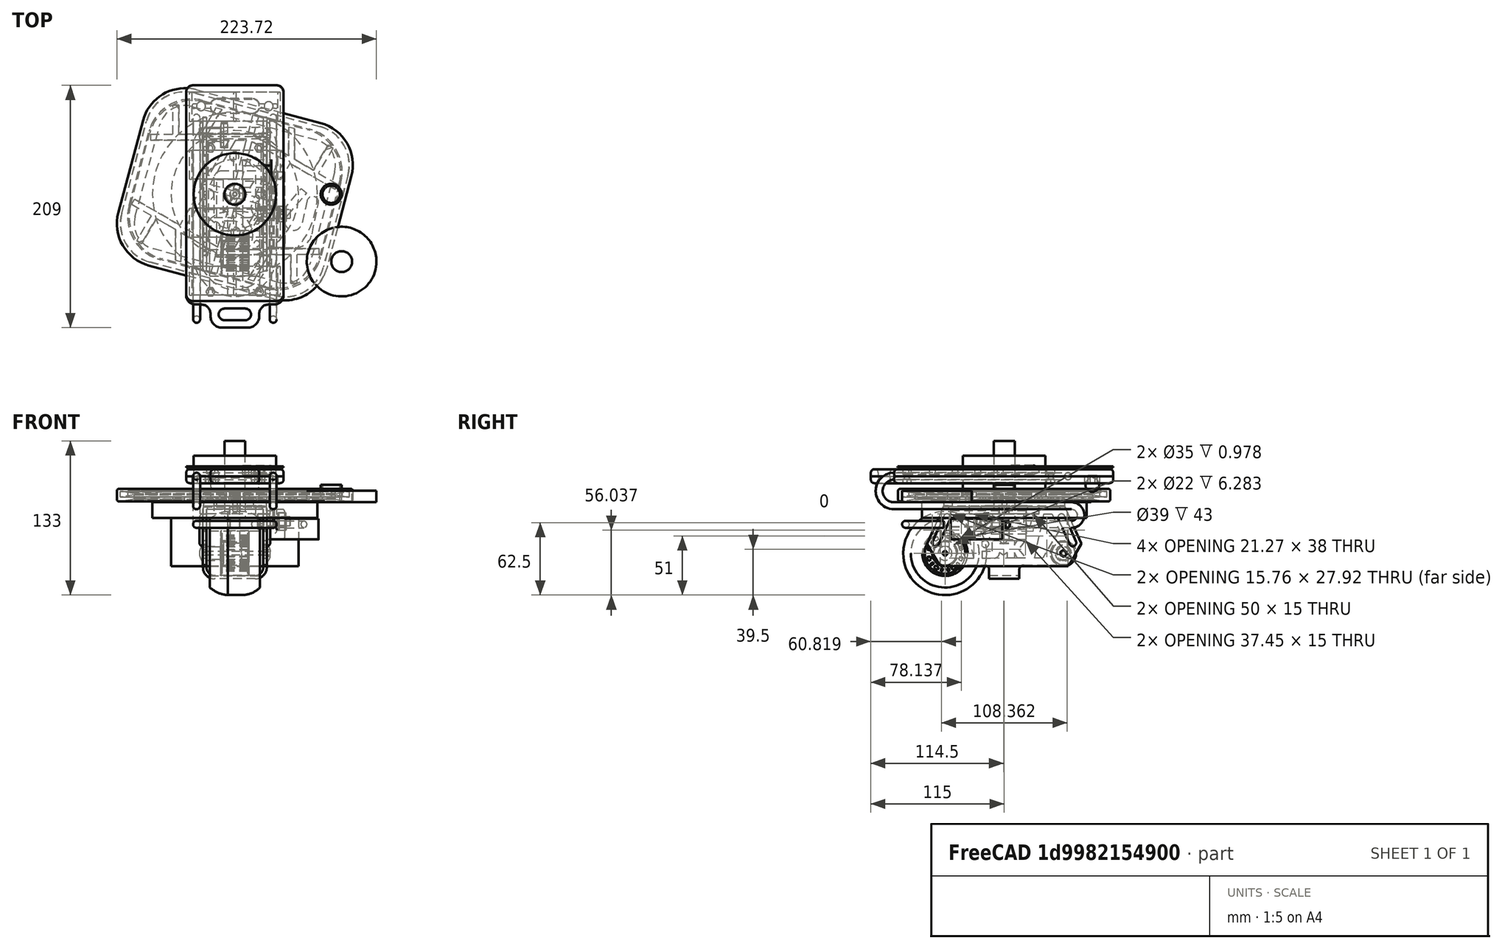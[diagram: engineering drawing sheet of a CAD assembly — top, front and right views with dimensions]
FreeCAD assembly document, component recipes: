
FREECAD ASSEMBLY — COMPONENT RECIPES ("freeskate")

This assembly document has 2 components, labeled P0..P1 below (a component is one placed body or linked part). 2 of them carry a construction recipe — the FreeCAD feature program that regenerates the part from scratch, quoted from this document or its linked companion documents; the rest are supplied as boundary geometry only. No exploded tour is included for this assembly.
COMPONENT P0 — recipe-attached ("freeskate001", modeled in this document).
Construction recipe (the document's own serialized feature program — sketch geometry with constraints, then the solid features built on it; lengths are millimeters unless a unit is written):

FEATURE [Sketcher::SketchObject] Sketch  label="plate-outline"
  ArcFitTolerance = 0
  AttachmentOffset = pos=(0,0,4.5) rot=(0,0,1;0rad)
  AttachmentSupport = -> [XY_Plane]
  FullyConstrained = true
  MakeInternals = false
  MapMode = 5
  Placement = pos=(0,0,4.5) rot=(0,0,1;0rad)
  sketch-geometry (8):
    g0: LineSegment StartX=-33 StartY=85.5 StartZ=0 EndX=33 EndY=85.5 EndZ=0
    g1: LineSegment StartX=71 StartY=47.5 StartZ=0 EndX=71 EndY=-47.5 EndZ=0
    g2: LineSegment StartX=33 StartY=-85.5 StartZ=0 EndX=-33 EndY=-85.5 EndZ=0
    g3: LineSegment StartX=-71 StartY=-47.5 StartZ=0 EndX=-71 EndY=47.5 EndZ=0
    g4: ArcOfCircle CenterX=-33 CenterY=47.5 CenterZ=0 NormalX=0 NormalY=0 NormalZ=1 AngleXU=0 Radius=38 StartAngle=1.5708 EndAngle=3.14159
    g5: ArcOfCircle CenterX=33 CenterY=47.5 CenterZ=0 NormalX=0 NormalY=0 NormalZ=1 AngleXU=0 Radius=38 StartAngle=0 EndAngle=1.5708
    g6: ArcOfCircle CenterX=33 CenterY=-47.5 CenterZ=0 NormalX=0 NormalY=0 NormalZ=1 AngleXU=0 Radius=38 StartAngle=4.71239 EndAngle=6.28319
    g7: ArcOfCircle CenterX=-33 CenterY=-47.5 CenterZ=0 NormalX=0 NormalY=0 NormalZ=1 AngleXU=0 Radius=38 StartAngle=3.14159 EndAngle=4.71239
  constraints (18):
    c: Horizontal(g2)
    c: Vertical(g3)
    c: Tangent(g0,g4) = 1.5708
    c: Tangent(g3,g4) = 1.5708
    c: Tangent(g0,g5) = 1.5708
    c: Tangent(g1,g5) = 1.5708
    c: Tangent(g1,g6) = 1.5708
    c: Tangent(g2,g6) = 1.5708
    c: Tangent(g2,g7) = 1.5708
    c: Tangent(g3,g7) = 1.5708
    c: DistanceY(g2,g0) = 171
    c: DistanceX(g3,g1) = 142
    c: Symmetric(g0,g2,g-1)
    c: Horizontal(g0)
    c: Symmetric(g3,g1,g-2)
    c: Vertical(g1)
    c: Radius(g5) = 38
    c: Radius(g6) = 38
FEATURE [PartDesign::Pad] Pad  label="plate-outline-pad"
  Direction = (0,0,1)
  Length = 5
  Length2 = 10
  Profile = -> Sketch
  ReferenceAxis = -> Sketch [N_Axis]
  Suppressed = false
  Type = 0
FEATURE [Sketcher::SketchObject] Sketch010  label="outline"
  ArcFitTolerance = 0
  AttachmentSupport = -> [XY_Plane002]
  FullyConstrained = true
  MakeInternals = false
  MapMode = 5
  sketch-geometry (6):
    g0: LineSegment StartX=16 StartY=52 StartZ=0 EndX=27 EndY=45 EndZ=0
    g1: LineSegment StartX=-27 StartY=52 StartZ=0 EndX=16 EndY=52 EndZ=0
    g2: LineSegment StartX=27 StartY=45 StartZ=0 EndX=27 EndY=-52 EndZ=0
    g3: LineSegment StartX=-27 StartY=-45 StartZ=0 EndX=-16 EndY=-52 EndZ=0
    g4: LineSegment StartX=-27 StartY=52 StartZ=0 EndX=-27 EndY=-45 EndZ=0
    g5: LineSegment StartX=-16 StartY=-52 StartZ=0 EndX=27 EndY=-52 EndZ=0
  constraints (18):
    c: Coincident(g1,g0)
    c: Horizontal(g1)
    c: Coincident(g2,g0)
    c: Vertical(g2)
    c: Coincident(g4,g1)
    c: Coincident(g4,g3)
    c: Vertical(g4)
    c: Coincident(g5,g3)
    c: Coincident(g5,g2)
    c: Horizontal(g5)
    c: DistanceY(g0,g0) = 7
    c: DistanceX(g0,g0) = 11
    c: DistanceX(g1,g-1) = 27
    c: DistanceX(g-1,g0) = 27
    c: DistanceX(g3,g3) = 11
    c: DistanceY(g3,g3) = 7
    c: DistanceY(g-1,g1) = 52
    c: DistanceY(g2,g-1) = 52
FEATURE [PartDesign::Pad] Pad003  label="outline-pad"
  Direction = (0,0,1)
  Length = 4
  Length2 = 10
  Profile = -> Sketch010
  ReferenceAxis = -> Sketch010 [N_Axis]
  Reversed = true
  Suppressed = false
  Type = 0
FEATURE [PartDesign::Body] Body002  label="shock-absorber"
  AllowCompound = false
  Group = -> [Sketch010,Pad003]
  Origin = -> Origin002
  Tip = -> Pad003
FEATURE [Sketcher::SketchObject] Sketch012  label="top-profile"
  ArcFitTolerance = 0
  AttachmentOffset = pos=(0,0,-44) rot=(0,0,1;0rad)
  FullyConstrained = false
  MakeInternals = false
  MapMode = 5
  Placement = pos=(0,51,-44) rot=(0,0,1;0rad)
  sketch-geometry (13):
    g0: LineSegment StartX=11.9778 StartY=-19.5 StartZ=0 EndX=-11.9778 EndY=-19.5 EndZ=0
    g1: LineSegment StartX=-11.9778 StartY=-19.5 StartZ=0 EndX=-11.9778 EndY=-17.5 EndZ=0
    g2: LineSegment StartX=-11.9778 StartY=-17.5 StartZ=0 EndX=-11 EndY=-17.5 EndZ=0
    g3: LineSegment StartX=-11 StartY=-17.5 StartZ=0 EndX=-12 EndY=-11 EndZ=0
    g4: LineSegment StartX=-12 StartY=-11 StartZ=0 EndX=-5.71671 EndY=-11 EndZ=0
    g5: LineSegment StartX=-5.71671 StartY=-11 StartZ=0 EndX=-5.71671 EndY=-10 EndZ=0
    g6: LineSegment StartX=-5.71671 StartY=-10 StartZ=0 EndX=5.71671 EndY=-10 EndZ=0
    g7: LineSegment StartX=5.71671 StartY=-10 StartZ=0 EndX=5.71671 EndY=-11 EndZ=0
    g8: LineSegment StartX=5.71671 StartY=-11 StartZ=0 EndX=12 EndY=-11 EndZ=0
    g9: LineSegment StartX=12 StartY=-11 StartZ=0 EndX=11 EndY=-17.5 EndZ=0
    g10: LineSegment StartX=11 StartY=-17.5 StartZ=0 EndX=11.9778 EndY=-17.5 EndZ=0
    g11: LineSegment StartX=11.9778 StartY=-17.5 StartZ=0 EndX=11.9778 EndY=-19.5 EndZ=0
    g12: GeomPoint [constr] X=0 Y=0 Z=0
  constraints (29):
    c: Coincident(g1,g0)
    c: Vertical(g1)
    c: Coincident(g2,g1)
    c: Horizontal(g2)
    c: Coincident(g3,g2)
    c: Horizontal(g4)
    c: Coincident(g5,g4)
    c: Vertical(g5)
    c: Coincident(g6,g5)
    c: Coincident(g7,g6)
    c: Coincident(g8,g7)
    c: Coincident(g9,g8)
    c: Coincident(g10,g9)
    c: Coincident(g11,g10)
    c: Coincident(g11,g0)
    c: Symmetric(g0,g0,g-2)
    c: Symmetric(g1,g10,g-2)
    c: Symmetric(g2,g9,g-2)
    c: Symmetric(g3,g8,g-2)
    c: Coincident(g3,g4)
    c: Symmetric(g4,g7,g-2)
    c: Symmetric(g5,g6,g-2)
    c: DistanceY(g0,g12) = 19.5
    c: DistanceX(g3,g8) = 24
    c: DistanceX(g3,g2) = 1
    c: DistanceY(g3,g12) = 11
    c: DistanceY(g5,g12) = 10
    c: DistanceY(g1,g1) = 2
    c: Coincident(g12,g-1)
FEATURE [Sketcher::SketchObject] Sketch018  label="rib-outlines"
  ArcFitTolerance = 0
  AttachmentSupport = -> [XY_Plane]
  FullyConstrained = true
  MakeInternals = false
  MapMode = 5
  sketch-geometry (29):
    g0: LineSegment StartX=-2.5 StartY=2.5 StartZ=0 EndX=-47.8236 EndY=2.5 EndZ=0
    g1: LineSegment StartX=-2.5 StartY=2.5 StartZ=0 EndX=-2.5 EndY=22.8798 EndZ=0
    g2: LineSegment StartX=0 StartY=28.726 StartZ=0 EndX=-38.0635 EndY=38.9251 EndZ=0
    g3: LineSegment StartX=-38.0635 StartY=38.9251 StartZ=0 EndX=-26.4167 EndY=82.3918 EndZ=0
    g4: LineSegment StartX=-31.2463 StartY=83.6859 StartZ=0 EndX=-26.4167 EndY=82.3918 EndZ=0
    g5: LineSegment StartX=-53 StartY=2.5 StartZ=0 EndX=-70 EndY=2.5 EndZ=0
    g6: LineSegment StartX=-70 StartY=2.5 StartZ=0 EndX=-70 EndY=0 EndZ=0
    g7: LineSegment StartX=-70 StartY=0 StartZ=0 EndX=0 EndY=0 EndZ=0
    g8: LineSegment StartX=0 StartY=0 StartZ=0 EndX=0 EndY=28.726 EndZ=0
    g9: LineSegment StartX=-39.3576 StartY=34.0955 StartZ=0 EndX=-43.952 EndY=16.9491 EndZ=0
    g10: LineSegment StartX=-43.952 StartY=16.9491 StartZ=0 EndX=-9.65926 EndY=26.1378 EndZ=0
    g11: LineSegment StartX=-9.65926 StartY=26.1378 StartZ=0 EndX=-39.3576 EndY=34.0955 EndZ=0
    g12: LineSegment StartX=-2.5 StartY=22.8798 StartZ=0 EndX=-45.4463 EndY=11.3723 EndZ=0
    g13: LineSegment StartX=-45.4463 StartY=11.3723 StartZ=0 EndX=-47.8236 EndY=2.5 EndZ=0
    g14: LineSegment StartX=-36.2863 StartY=64.8764 StartZ=0 EndX=-60.4344 EndY=71.3469 EndZ=0
    g15: LineSegment StartX=-60.4344 StartY=71.3469 StartZ=0 EndX=-61.7285 EndY=66.5172 EndZ=0
    g16: LineSegment StartX=-61.7285 StartY=66.5172 StartZ=0 EndX=-37.5804 EndY=60.0467 EndZ=0
    g17: LineSegment StartX=-42.498 StartY=41.6942 StartZ=0 EndX=-68 EndY=34.8609 EndZ=0
    g18: LineSegment StartX=-68 StartY=34.8609 StartZ=0 EndX=-68 EndY=29.8609 EndZ=0
    g19: LineSegment StartX=-68 StartY=29.8609 StartZ=0 EndX=-43.9413 EndY=36.3074 EndZ=0
    g20: LineSegment StartX=-31.2463 StartY=83.6859 StartZ=0 EndX=-36.2863 EndY=64.8764 EndZ=0
    g21: LineSegment StartX=-37.5804 StartY=60.0467 StartZ=0 EndX=-42.498 EndY=41.6942 EndZ=0
    g22: LineSegment StartX=-43.9413 StartY=36.3074 StartZ=0 EndX=-53 EndY=2.5 EndZ=0
    g23: LineSegment [constr] StartX=-31.2463 StartY=83.6859 StartZ=0 EndX=-53 EndY=2.5 EndZ=0
    g24: LineSegment [constr] StartX=-26.4167 StartY=82.3918 StartZ=0 EndX=-47.8236 EndY=2.5 EndZ=0
    g25: LineSegment [constr] StartX=-43.952 StartY=16.9491 StartZ=0 EndX=-49.5288 EndY=15.4548 EndZ=0
    g26: LineSegment [constr] StartX=-53 StartY=2.5 StartZ=0 EndX=-53.6699 EndY=0 EndZ=0
    g27: LineSegment [constr] StartX=-9.65926 StartY=26.1378 StartZ=0 EndX=0 EndY=28.726 EndZ=0
    g28: LineSegment [constr] StartX=-43.952 StartY=16.9491 StartZ=0 EndX=-42.6579 EndY=12.1195 EndZ=0
  constraints (83):
    c: Horizontal(g0)
    c: Coincident(g1,g0)
    c: Vertical(g1)
    c: PointOnObject(g2,g-2)
    c: Coincident(g3,g2)
    c: Coincident(g4,g3)
    c: Horizontal(g5)
    c: Coincident(g6,g5)
    c: PointOnObject(g6,g-1)
    c: Vertical(g6)
    c: Coincident(g7,g6)
    c: Coincident(g7,g-1)
    c: Coincident(g8,g7)
    c: Coincident(g8,g2)
    c: Coincident(g10,g9)
    c: Coincident(g11,g10)
    c: Coincident(g11,g9)
    c: Coincident(g12,g1)
    c: Coincident(g13,g12)
    c: Coincident(g13,g0)
    c: Coincident(g15,g14)
    c: Coincident(g16,g15)
    c: Coincident(g18,g17)
    c: Coincident(g19,g18)
    c: Coincident(g20,g4)
    c: Coincident(g20,g14)
    c: Coincident(g21,g16)
    c: Coincident(g21,g17)
    c: Coincident(g22,g19)
    c: Coincident(g22,g5)
    c: DistanceY(g6,g6) = 2.5
    c: Horizontal(g5,g0)
    c: Angle(g20,g4) = 1.5708
    c: Coincident(g23,g4)
    c: Coincident(g23,g5)
    c: Coincident(g24,g3)
    c: Coincident(g24,g0)
    c: PointOnObject(g14,g23)
    c: PointOnObject(g16,g23)
    c: PointOnObject(g17,g23)
    c: PointOnObject(g19,g23)
    c: PointOnObject(g12,g24)
    c: PointOnObject(g9,g24)
    c: PointOnObject(g2,g24)
    c: Distance(g14,g16) = 5
    c: Angle(g20,g14) = 1.5708
    c: Parallel(g14,g16)
    c: Angle(g15,g14) = 1.5708
    c: Vertical(g18)
    c: DistanceY(g18,g18) = 5
    c: Parallel(g17,g19)
    c: Distance(g2,g9) = 5
    c: Parallel(g11,g2)
    c: PointOnObject(g9,g24)
    c: Parallel(g10,g12)
    c: Distance(g4) = 5
    c: Angle(g2,g3) = 1.5708
    c: Parallel(g23,g24)
    c: DistanceX(g17,g2) = 68
    c: DistanceX(g5,g7) = 53
    c: DistanceX(g7,g7) = 70
    c: Angle(g10,g9) = 1.0472
    c: Coincident(g25,g9)
    c: PointOnObject(g25,g22)
    c: Parallel(g25,g10)
    c: Coincident(g26,g5)
    c: PointOnObject(g26,g7)
    c: Parallel(g22,g26)
    c: Distance(g26,g25) = 16
    c: Coincident(g27,g10)
    c: Coincident(g27,g2)
    c: Parallel(g10,g27)
    c: Angle(g21,g17) = 2.0944
    c: Distance(g22) = 35
    c: Distance(g21) = 19
    c: Angle(g2,g8) = 1.8326
    c: DistanceX(g0,g7) = 2.5
    c: Coincident(g28,g9)
    c: PointOnObject(g28,g12)
    c: Angle(g28,g10) = 1.5708
    c: Distance(g28) = 5
    c: Distance(g16) = 25
    c: Distance(g3) = 45
FEATURE [PartDesign::Pad] Pad007  label="rib-outlines-pad"
  BaseFeature = -> Pad
  Direction = (0,0,1)
  Length = 4.5
  Length2 = 10
  Profile = -> Sketch018
  ReferenceAxis = -> Sketch018 [N_Axis]
  Suppressed = false
  Type = 0
FEATURE [PartDesign::Mirrored] Mirrored
  MirrorPlane = -> Sketch018 [V_Axis]
  Suppressed = false
  TransformMode = 0
FEATURE [PartDesign::Mirrored] Mirrored001
  MirrorPlane = -> XZ_Plane
  Suppressed = false
  TransformMode = 0
FEATURE [PartDesign::MultiTransform] MultiTransform
  BaseFeature = -> Pad007
  Originals = -> [Pad007]
  Suppressed = false
  TransformMode = 0
  Transformations = -> [Mirrored,Mirrored001]
FEATURE [Sketcher::SketchObject] Sketch019  label="grip-tape-inset"
  ArcFitTolerance = 0
  AttachmentOffset = pos=(0,0,9.5) rot=(0,0,1;0rad)
  AttachmentSupport = -> [XY_Plane]
  FullyConstrained = true
  MakeInternals = false
  MapMode = 5
  Placement = pos=(0,0,9.5) rot=(0,0,1;0rad)
  sketch-geometry (16):
    g0: LineSegment [constr] StartX=-71 StartY=85.5 StartZ=0 EndX=71 EndY=85.5 EndZ=0
    g1: LineSegment [constr] StartX=71 StartY=85.5 StartZ=0 EndX=71 EndY=-85.5 EndZ=0
    g2: LineSegment [constr] StartX=71 StartY=-85.5 StartZ=0 EndX=-71 EndY=-85.5 EndZ=0
    g3: LineSegment [constr] StartX=-71 StartY=-85.5 StartZ=0 EndX=-71 EndY=85.5 EndZ=0
    g4: LineSegment StartX=-32 StartY=84.5 StartZ=0 EndX=32 EndY=84.5 EndZ=0
    g5: LineSegment StartX=70 StartY=46.5 StartZ=0 EndX=70 EndY=-46.5 EndZ=0
    g6: LineSegment StartX=32 StartY=-84.5 StartZ=0 EndX=-32 EndY=-84.5 EndZ=0
    g7: LineSegment StartX=-70 StartY=-46.5 StartZ=0 EndX=-70 EndY=46.5 EndZ=0
    g8: ArcOfCircle CenterX=-32 CenterY=46.5 CenterZ=0 NormalX=0 NormalY=0 NormalZ=1 AngleXU=0 Radius=38 StartAngle=1.5708 EndAngle=3.14159
    g9: GeomPoint [constr] X=-70 Y=84.5 Z=0
    g10: ArcOfCircle CenterX=-32 CenterY=-46.5 CenterZ=0 NormalX=0 NormalY=0 NormalZ=1 AngleXU=0 Radius=38 StartAngle=3.14159 EndAngle=4.71239
    g11: GeomPoint [constr] X=-70 Y=-84.5 Z=0
    g12: ArcOfCircle CenterX=32 CenterY=-46.5 CenterZ=0 NormalX=0 NormalY=0 NormalZ=1 AngleXU=0 Radius=38 StartAngle=4.71239 EndAngle=6.28319
    g13: GeomPoint [constr] X=70 Y=-84.5 Z=0
    g14: ArcOfCircle CenterX=32 CenterY=46.5 CenterZ=0 NormalX=0 NormalY=0 NormalZ=1 AngleXU=0 Radius=38 StartAngle=0 EndAngle=1.5708
    g15: GeomPoint [constr] X=70 Y=84.5 Z=0
  constraints (36):
    c: Coincident(g0,g1)
    c: Coincident(g1,g2)
    c: Coincident(g2,g3)
    c: Coincident(g3,g0)
    c: Horizontal(g2)
    c: Vertical(g3)
    c: DistanceX(g0,g0) = 142
    c: DistanceY(g1,g1) = 171
    c: Symmetric(g0,g0,g-2)
    c: Symmetric(g0,g1,g-1)
    c: Horizontal(g6)
    c: Vertical(g5)
    c: DistanceX(g2,g11) = 1
    c: DistanceY(g2,g11) = 1
    c: Symmetric(g9,g11,g-1)
    c: Symmetric(g9,g15,g-2)
    c: PointOnObject(g9,g4)
    c: PointOnObject(g9,g7)
    c: Tangent(g4,g8) = 1.5708
    c: Tangent(g7,g8) = 1.5708
    c: PointOnObject(g11,g6)
    c: PointOnObject(g11,g7)
    c: Tangent(g6,g10) = 1.5708
    c: Tangent(g7,g10) = 1.5708
    c: PointOnObject(g13,g5)
    c: PointOnObject(g13,g6)
    c: Tangent(g5,g12) = 1.5708
    c: Tangent(g6,g12) = 1.5708
    c: PointOnObject(g15,g4)
    c: PointOnObject(g15,g5)
    c: Tangent(g4,g14) = 1.5708
    c: Tangent(g5,g14) = 1.5708
    c: Radius(g8) = 38
    c: Radius(g14) = 38
    c: Radius(g12) = 38
    c: Radius(g10) = 38
FEATURE [PartDesign::Pocket] Pocket  label="grip-tape-inset-pocket"
  BaseFeature = -> MultiTransform
  Direction = (0,0,-1)
  Length = 0.5
  Length2 = 5
  Profile = -> Sketch019
  ReferenceAxis = -> Sketch019 [N_Axis]
  Suppressed = false
  Type = 0
FEATURE [Sketcher::SketchObject] Sketch020  label="ribs-taper-y"
  ArcFitTolerance = 0
  AttachmentSupport = -> [YZ_Plane]
  FullyConstrained = true
  MakeInternals = false
  MapMode = 5
  Placement = pos=(0,0,0) rot=(0.57735,0.57735,0.57735;2.0944rad)
  sketch-geometry (10):
    g0: LineSegment StartX=-84 StartY=4.5 StartZ=0 EndX=-46.7137 EndY=0.197732 EndZ=0
    g1: LineSegment StartX=46.7137 StartY=0.197732 StartZ=0 EndX=84 EndY=4.5 EndZ=0
    g2: LineSegment StartX=-43.275 StartY=0 StartZ=0 EndX=43.275 EndY=0 EndZ=0
    g3: LineSegment StartX=-84 StartY=4.5 StartZ=0 EndX=-84 EndY=-7.5 EndZ=0
    g4: LineSegment StartX=-84 StartY=-7.5 StartZ=0 EndX=84 EndY=-7.5 EndZ=0
    g5: LineSegment StartX=84 StartY=-7.5 StartZ=0 EndX=84 EndY=4.5 EndZ=0
    g6: ArcOfCircle CenterX=43.275 CenterY=30 CenterZ=0 NormalX=0 NormalY=0 NormalZ=1 AngleXU=0 Radius=30 StartAngle=4.71239 EndAngle=4.82727
    g7: GeomPoint [constr] X=45 Y=0 Z=0
    g8: ArcOfCircle CenterX=-43.275 CenterY=30 CenterZ=0 NormalX=0 NormalY=0 NormalZ=1 AngleXU=0 Radius=30 StartAngle=4.59751 EndAngle=4.71239
    g9: GeomPoint [constr] X=-45 Y=0 Z=0
  constraints (24):
    c: Symmetric(g0,g1,g-2)
    c: Symmetric(g9,g7,g-2)
    c: PointOnObject(g9,g-1)
    c: DistanceY(g9,g0) = 4.5
    c: Coincident(g3,g0)
    c: Vertical(g3)
    c: Coincident(g4,g3)
    c: Horizontal(g4)
    c: Coincident(g5,g4)
    c: Coincident(g5,g1)
    c: Vertical(g5)
    c: DistanceY(g3,g3) = 12
    c: DistanceX(g0,g1) = 168
    c: DistanceX(g9,g7) = 90
    c: PointOnObject(g7,g1)
    c: PointOnObject(g7,g2)
    c: Tangent(g1,g6) = -1.5708
    c: Tangent(g2,g6) = -1.5708
    c: Radius(g6) = 30
    c: PointOnObject(g9,g0)
    c: PointOnObject(g9,g2)
    c: Tangent(g0,g8) = -1.5708
    c: Tangent(g2,g8) = -1.5708
    c: Radius(g8) = 30
FEATURE [PartDesign::Pocket] Pocket003  label="ribs-taper-y-pocket"
  BaseFeature = -> Pocket
  Direction = (-1,0,0)
  Length = 180
  Length2 = 5
  Midplane = true
  Profile = -> Sketch020
  ReferenceAxis = -> Sketch020 [N_Axis]
  Suppressed = false
  Type = 0
FEATURE [Sketcher::SketchObject] Sketch021  label="ribs-taper-x"
  ArcFitTolerance = 0
  AttachmentSupport = -> [XZ_Plane]
  FullyConstrained = true
  MakeInternals = false
  MapMode = 5
  Placement = pos=(0,0,0) rot=(1,0,0;1.5708rad)
  sketch-geometry (10):
    g0: LineSegment StartX=-71 StartY=4.5 StartZ=0 EndX=-47.5392 EndY=0.439485 EndZ=0
    g1: LineSegment StartX=-42.423 StartY=0 StartZ=0 EndX=42.423 EndY=0 EndZ=0
    g2: LineSegment StartX=47.5392 StartY=0.439485 StartZ=0 EndX=71 EndY=4.5 EndZ=0
    g3: LineSegment StartX=71 StartY=4.5 StartZ=0 EndX=71 EndY=-7.5 EndZ=0
    g4: LineSegment StartX=71 StartY=-7.5 StartZ=0 EndX=-71 EndY=-7.5 EndZ=0
    g5: LineSegment StartX=-71 StartY=-7.5 StartZ=0 EndX=-71 EndY=4.5 EndZ=0
    g6: ArcOfCircle CenterX=42.423 CenterY=30 CenterZ=0 NormalX=0 NormalY=0 NormalZ=1 AngleXU=0 Radius=30 StartAngle=4.71239 EndAngle=4.88377
    g7: GeomPoint [constr] X=45 Y=0 Z=0
    g8: ArcOfCircle CenterX=-42.423 CenterY=30 CenterZ=0 NormalX=0 NormalY=0 NormalZ=1 AngleXU=0 Radius=30 StartAngle=4.54101 EndAngle=4.71239
    g9: GeomPoint [constr] X=-45 Y=0 Z=0
  constraints (24):
    c: PointOnObject(g9,g-1)
    c: Coincident(g3,g2)
    c: Vertical(g3)
    c: Coincident(g4,g3)
    c: Horizontal(g4)
    c: Coincident(g5,g4)
    c: Coincident(g5,g0)
    c: Vertical(g5)
    c: Symmetric(g0,g2,g-2)
    c: DistanceY(g5,g5) = 12
    c: DistanceY(g9,g0) = 4.5
    c: DistanceX(g9,g7) = 90
    c: DistanceX(g0,g2) = 142
    c: Symmetric(g9,g7,g-2)
    c: PointOnObject(g7,g1)
    c: PointOnObject(g7,g2)
    c: Tangent(g1,g6) = -1.5708
    c: Tangent(g2,g6) = -1.5708
    c: Radius(g6) = 30
    c: PointOnObject(g9,g0)
    c: PointOnObject(g9,g1)
    c: Tangent(g0,g8) = -1.5708
    c: Tangent(g1,g8) = -1.5708
    c: Radius(g8) = 30
FEATURE [PartDesign::Pocket] Pocket004  label="ribs-taper-x-pocket"
  BaseFeature = -> Pocket003
  Direction = (0,1,-2e-16)
  Length = 150
  Length2 = 5
  Midplane = true
  Profile = -> Sketch021
  ReferenceAxis = -> Sketch021 [N_Axis]
  Suppressed = false
  Type = 0
FEATURE [PartDesign::FeatureBase] BaseFeature
  BaseFeature = -> Cut001
  Suppressed = false
FEATURE [Sketcher::SketchObject] Sketch032  label="grind-spline-outline"
  ArcFitTolerance = 0
  AttachmentOffset = pos=(49.3,-13,27.5) rot=(0,0,1;0.418879rad)
  AttachmentSupport = -> [YZ_Plane007]
  FullyConstrained = true
  MakeInternals = false
  MapMode = 5
  Placement = pos=(27.5,49.3,-13) rot=(0.642595,0.417306,0.642595;2.35092rad)
  sketch-geometry (4):
    g0: LineSegment StartX=3 StartY=0 StartZ=0 EndX=3 EndY=-24 EndZ=0
    g1: ArcOfCircle CenterX=0 CenterY=0 CenterZ=0 NormalX=0 NormalY=0 NormalZ=1 AngleXU=0 Radius=3 StartAngle=0 EndAngle=1.5708
    g2: ArcOfCircle CenterX=0 CenterY=-24 CenterZ=0 NormalX=0 NormalY=0 NormalZ=1 AngleXU=0 Radius=3 StartAngle=4.71239 EndAngle=6.28319
    g3: LineSegment StartX=2e-16 StartY=3 StartZ=0 EndX=-6e-16 EndY=-27 EndZ=0
  constraints (13):
    c: PointOnObject(g0,g-1)
    c: Vertical(g0)
    c: Coincident(g1,g-1)
    c: Coincident(g1,g0)
    c: PointOnObject(g1,g-2)
    c: PointOnObject(g2,g-2)
    c: Coincident(g2,g0)
    c: PointOnObject(g2,g-2)
    c: Horizontal(g2,g0)
    c: DistanceX(g1,g0) = 3
    c: DistanceY(g2,g1) = 30
    c: Coincident(g3,g1)
    c: Coincident(g3,g2)
FEATURE [PartDesign::Revolution] Revolution  label="grind-spline-revolution"
  Angle = 180
  Angle2 = 60
  Axis = (0,-0.406737,0.913545)
  Base = (27.5,49.3,-13)
  BaseFeature = -> BaseFeature
  Profile = -> Sketch032
  ReferenceAxis = -> Sketch032 [V_Axis]
  Reversed = true
  Suppressed = false
  Type = 0
FEATURE [PartDesign::Mirrored] Mirrored003  label="grind-spline-mirror-y"
  MirrorPlane = -> XZ_Plane007
  Suppressed = false
  TransformMode = 0
FEATURE [PartDesign::Mirrored] Mirrored004  label="grind-spline-mirror-x"
  MirrorPlane = -> YZ_Plane007
  Suppressed = false
  TransformMode = 0
FEATURE [PartDesign::MultiTransform] MultiTransform001  label="grind-spline-mirroring"
  BaseFeature = -> Revolution
  Originals = -> [Revolution]
  Suppressed = false
  TransformMode = 0
  Transformations = -> [Mirrored003,Mirrored004]
FEATURE [PartDesign::Body] Body006  label="chassis"
  AllowCompound = false
  BaseFeature = -> Cut001
  Group = -> [BaseFeature,Sketch032,Revolution,MultiTransform001,Mirrored003,Mirrored004]
  Origin = -> Origin007
  Tip = -> MultiTransform001
FEATURE [Sketcher::SketchObject] Sketch035
  ArcFitTolerance = 0
  AttachmentSupport = -> [YZ_Plane008]
  FullyConstrained = true
  MakeInternals = false
  MapMode = 5
  Placement = pos=(0,0,0) rot=(0.57735,0.57735,0.57735;2.0944rad)
  sketch-geometry (2):
    g0: Circle CenterX=0 CenterY=0 CenterZ=0 NormalX=0 NormalY=0 NormalZ=1 AngleXU=0 Radius=10
    g1: Circle CenterX=0 CenterY=0 CenterZ=0 NormalX=0 NormalY=0 NormalZ=1 AngleXU=0 Radius=11
  constraints (4):
    c: Coincident(g0,g-1)
    c: Coincident(g1,g0)
    c: Diameter(g1) = 22
    c: Diameter(g0) = 20
FEATURE [PartDesign::Pad] Pad013
  Direction = (1,0,0)
  Length = 6
  Length2 = 10
  Placement = pos=(0,0,0) rot=(1,1,1;2.0944rad)
  Profile = -> Sketch035
  ReferenceAxis = -> Sketch035 [N_Axis]
  Suppressed = false
  Type = 0
FEATURE [PartDesign::Body] Body007  label="bearing-outer-front-left"
  AllowCompound = false
  Group = -> [Sketch035,Pad013]
  Origin = -> Origin008
  Placement = pos=(6,-51,-44) rot=(0,0,1;0rad)
  Tip = -> Pad013
FEATURE [Sketcher::SketchObject] Sketch036
  ArcFitTolerance = 0
  AttachmentSupport = -> [XY_Plane009]
  FullyConstrained = true
  MakeInternals = false
  MapMode = 5
  sketch-geometry (4):
    g0: LineSegment StartX=-24.5 StartY=6 StartZ=0 EndX=-12.5 EndY=6 EndZ=0
    g1: LineSegment StartX=-12.5 StartY=6 StartZ=0 EndX=-12.5 EndY=5.5 EndZ=0
    g2: LineSegment StartX=-12.5 StartY=5.5 StartZ=0 EndX=-24.5 EndY=5.5 EndZ=0
    g3: LineSegment StartX=-24.5 StartY=5.5 StartZ=0 EndX=-24.5 EndY=6 EndZ=0
  constraints (12):
    c: Coincident(g0,g1)
    c: Coincident(g1,g2)
    c: Coincident(g2,g3)
    c: Coincident(g3,g0)
    c: Horizontal(g2)
    c: Vertical(g1)
    c: Vertical(g3)
    c: DistanceY(g-1,g0) = 6
    c: DistanceX(g0,g0) = 12
    c: DistanceY(g1,g1) = 0.5
    c: Horizontal(g0,g0)
    c: DistanceX(g0,g-1) = 24.5
FEATURE [PartDesign::Revolution] Revolution001
  Angle = 360
  Angle2 = 60
  Axis = (1,0,0)
  Base = (0,0,0)
  Profile = -> Sketch036
  ReferenceAxis = -> X_Axis009
  Suppressed = false
  Type = 0
FEATURE [PartDesign::Body] Body008  label="washer"
  AllowCompound = false
  Group = -> [Sketch036,Revolution001]
  Origin = -> Origin009
  Placement = pos=(0,-51,-44) rot=(0,0,1;0rad)
  Tip = -> Revolution001
FEATURE [PartDesign::Revolution] Revolution002
  Angle = 360
  Angle2 = 60
  Axis = (1,0,0)
  Base = (0,51,-44)
  Placement = pos=(0,51,-44) rot=(0,0,1;0rad)
  Profile = -> Sketch012
  ReferenceAxis = -> Sketch012 [H_Axis]
  Suppressed = false
  Type = 0
FEATURE [Sketcher::SketchObject] Sketch037
  ArcFitTolerance = 0
  AttachmentOffset = pos=(51,-44,0) rot=(0,0,1;0rad)
  AttachmentSupport = -> [YZ_Plane010]
  FullyConstrained = false
  MakeInternals = false
  MapMode = 5
  Placement = pos=(0,51,-44) rot=(0.57735,0.57735,0.57735;2.0944rad)
  sketch-geometry (26):
    g0: Circle [constr] CenterX=0 CenterY=0 CenterZ=0 NormalX=0 NormalY=0 NormalZ=1 AngleXU=0 Radius=15.7365
    g1: Circle [constr] CenterX=0 CenterY=0 CenterZ=0 NormalX=0 NormalY=0 NormalZ=1 AngleXU=0 Radius=13.1538
    g2: ArcOfCircle CenterX=0 CenterY=0 CenterZ=0 NormalX=0 NormalY=0 NormalZ=1 AngleXU=0 Radius=15.7365 StartAngle=0.908509 EndAngle=1.14653
    g3: ArcOfCircle CenterX=0 CenterY=0 CenterZ=0 NormalX=0 NormalY=0 NormalZ=1 AngleXU=0 Radius=13.1538 StartAngle=0.908509 EndAngle=1.14653
    g4: LineSegment [constr] StartX=6.47794 StartY=14.3413 StartZ=0 EndX=0 EndY=0 EndZ=0
    g5: LineSegment [constr] StartX=9.67673 StartY=12.4096 StartZ=0 EndX=0 EndY=0 EndZ=0
    g6: LineSegment StartX=6.47794 StartY=14.3413 StartZ=0 EndX=5.41477 EndY=11.9876 EndZ=0
    g7: LineSegment StartX=9.67673 StartY=12.4096 StartZ=0 EndX=8.08858 EndY=10.3729 EndZ=0
    g8: ArcOfCircle CenterX=0 CenterY=0 CenterZ=0 NormalX=0 NormalY=0 NormalZ=1 AngleXU=0 Radius=15.7365 StartAngle=0.627933 EndAngle=0.735551
    g9: ArcOfCircle CenterX=0 CenterY=0 CenterZ=0 NormalX=0 NormalY=0 NormalZ=1 AngleXU=0 Radius=13.1538 StartAngle=0.627933 EndAngle=0.735551
    g10: LineSegment [constr] StartX=11.668 StartY=10.5591 StartZ=0 EndX=0 EndY=0 EndZ=0
    g11: LineSegment [constr] StartX=12.7347 StartY=9.24478 StartZ=0 EndX=0 EndY=0 EndZ=0
    g12: LineSegment StartX=11.668 StartY=10.5591 StartZ=0 EndX=9.75305 EndY=8.82616 EndZ=0
    g13: LineSegment StartX=12.7347 StartY=9.24478 StartZ=0 EndX=10.6446 EndY=7.72751 EndZ=0
    g14: ArcOfCircle CenterX=0 CenterY=0 CenterZ=0 NormalX=0 NormalY=0 NormalZ=1 AngleXU=0 Radius=15.7365 StartAngle=1.32792 EndAngle=1.44265
    g15: ArcOfCircle CenterX=0 CenterY=0 CenterZ=0 NormalX=0 NormalY=0 NormalZ=1 AngleXU=0 Radius=13.1538 StartAngle=1.32792 EndAngle=1.44265
    g16: LineSegment [constr] StartX=2.01101 StartY=15.6075 StartZ=0 EndX=0 EndY=0 EndZ=0
    g17: LineSegment [constr] StartX=3.78452 StartY=15.2747 StartZ=0 EndX=0 EndY=0 EndZ=0
    g18: LineSegment StartX=2.01101 StartY=15.6075 StartZ=0 EndX=1.68096 EndY=13.046 EndZ=0
    g19: LineSegment StartX=3.78452 StartY=15.2747 StartZ=0 EndX=3.1634 EndY=12.7678 EndZ=0
    g20: ArcOfCircle CenterX=0 CenterY=0 CenterZ=0 NormalX=0 NormalY=0 NormalZ=1 AngleXU=0 Radius=15.7365 StartAngle=0.197299 EndAngle=0.428307
    g21: ArcOfCircle CenterX=0 CenterY=0 CenterZ=0 NormalX=0 NormalY=0 NormalZ=1 AngleXU=0 Radius=13.1538 StartAngle=0.197299 EndAngle=0.428307
    g22: LineSegment [constr] StartX=14.315 StartY=6.53586 StartZ=0 EndX=0 EndY=0 EndZ=0
    g23: LineSegment [constr] StartX=15.4312 StartY=3.08469 StartZ=0 EndX=0 EndY=0 EndZ=0
    g24: LineSegment StartX=14.315 StartY=6.53586 StartZ=0 EndX=11.9656 EndY=5.46319 EndZ=0
    g25: LineSegment StartX=15.4312 StartY=3.08469 StartZ=0 EndX=12.8986 EndY=2.57843 EndZ=0
  constraints (58):
    c: Coincident(g0,g-1)
    c: Coincident(g1,g0)
    c: Coincident(g2,g0)
    c: PointOnObject(g2,g0)
    c: Coincident(g3,g2)
    c: PointOnObject(g3,g1)
    c: Coincident(g4,g2)
    c: Coincident(g4,g2)
    c: Coincident(g5,g2)
    c: PointOnObject(g3,g4)
    c: PointOnObject(g3,g5)
    c: Coincident(g6,g2)
    c: Coincident(g6,g3)
    c: Coincident(g7,g2)
    c: Coincident(g7,g3)
    c: Coincident(g8,g2)
    c: PointOnObject(g8,g0)
    c: Coincident(g9,g2)
    c: PointOnObject(g9,g1)
    c: Coincident(g10,g8)
    c: Coincident(g10,g2)
    c: Coincident(g11,g8)
    c: Coincident(g11,g5)
    c: PointOnObject(g9,g10)
    c: PointOnObject(g9,g11)
    c: Coincident(g12,g8)
    c: Coincident(g12,g9)
    c: Coincident(g13,g8)
    c: Coincident(g13,g9)
    c: Coincident(g14,g2)
    c: PointOnObject(g14,g0)
    c: Coincident(g15,g2)
    c: PointOnObject(g15,g1)
    c: Coincident(g16,g14)
    c: Coincident(g16,g2)
    c: Coincident(g17,g14)
    c: Coincident(g17,g5)
    c: PointOnObject(g15,g16)
    c: PointOnObject(g15,g17)
    c: Coincident(g18,g14)
    c: Coincident(g18,g15)
    c: Coincident(g19,g14)
    c: Coincident(g19,g15)
    c: Coincident(g5,g2)
    c: Coincident(g20,g2)
    c: PointOnObject(g20,g0)
    c: Coincident(g21,g2)
    c: PointOnObject(g21,g1)
    c: Coincident(g22,g20)
    c: Coincident(g22,g2)
    c: Coincident(g23,g20)
    c: Coincident(g23,g2)
    c: PointOnObject(g21,g22)
    c: PointOnObject(g21,g23)
    c: Coincident(g24,g20)
    c: Coincident(g24,g21)
    c: Coincident(g25,g20)
    c: Coincident(g25,g21)
FEATURE [PartDesign::Pocket] Pocket008
  BaseFeature = -> Revolution002
  Direction = (-1,0,0)
  Length = 50
  Length2 = 5
  Midplane = true
  Placement = pos=(0,51,-44) rot=(0,0,1;0rad)
  Profile = -> Sketch037
  ReferenceAxis = -> Sketch037 [N_Axis]
  Suppressed = false
  Type = 0
FEATURE [PartDesign::Mirrored] Mirrored007
  MirrorPlane = -> Sketch037 [V_Axis]
  Placement = pos=(0,51,-44) rot=(0,0,1;0rad)
  Suppressed = false
  TransformMode = 0
FEATURE [PartDesign::Mirrored] Mirrored008
  MirrorPlane = -> Sketch037 [H_Axis]
  Placement = pos=(0,51,-44) rot=(0,0,1;0rad)
  Suppressed = false
  TransformMode = 0
FEATURE [PartDesign::MultiTransform] MultiTransform002
  BaseFeature = -> Pocket008
  Originals = -> [Pocket008]
  Placement = pos=(0,51,-44) rot=(0,0,1;0rad)
  Suppressed = false
  TransformMode = 0
  Transformations = -> [Mirrored007,Mirrored008]
FEATURE [PartDesign::Body] Body009  label="wheel-inner-back"
  AllowCompound = false
  Group = -> [Sketch012,Revolution002,Sketch037,Pocket008,MultiTransform002,Mirrored007,Mirrored008]
  Origin = -> Origin010
  Tip = -> MultiTransform002
FEATURE [Sketcher::SketchObject] Sketch038
  ArcFitTolerance = 0
  AttachmentSupport = -> [YZ_Plane011]
  FullyConstrained = true
  MakeInternals = false
  MapMode = 5
  Placement = pos=(0,0,0) rot=(0.57735,0.57735,0.57735;2.0944rad)
  sketch-geometry (2):
    g0: Circle CenterX=0 CenterY=0 CenterZ=0 NormalX=0 NormalY=0 NormalZ=1 AngleXU=0 Radius=10
    g1: Circle CenterX=0 CenterY=0 CenterZ=0 NormalX=0 NormalY=0 NormalZ=1 AngleXU=0 Radius=6
  constraints (4):
    c: Coincident(g0,g-1)
    c: Coincident(g1,g0)
    c: Diameter(g0) = 20
    c: Diameter(g1) = 12
FEATURE [PartDesign::Pad] Pad014
  Direction = (1,0,0)
  Length = 2
  Length2 = 10
  Placement = pos=(0,0,0) rot=(1,1,1;2.0944rad)
  Profile = -> Sketch038
  ReferenceAxis = -> Sketch038 [N_Axis]
  Suppressed = false
  Type = 0
FEATURE [PartDesign::Body] Body010  label="bearing-inner-back-left"
  AllowCompound = false
  Group = -> [Sketch038,Pad014]
  Origin = -> Origin011
  Placement = pos=(10,51,-44) rot=(0,0,1;0rad)
  Tip = -> Pad014
FEATURE [Sketcher::SketchObject] Sketch048  label="bolt-holes"
  ArcFitTolerance = 0
  AttachmentOffset = pos=(0,0,9) rot=(0,0,1;0rad)
  AttachmentSupport = -> [XY_Plane]
  FullyConstrained = true
  MakeInternals = false
  MapMode = 5
  Placement = pos=(0,0,9) rot=(0,0,1;0rad)
  sketch-geometry (4):
    g0: Circle CenterX=-31.25 CenterY=9 CenterZ=0 NormalX=0 NormalY=0 NormalZ=1 AngleXU=0 Radius=4
    g1: Circle CenterX=31.25 CenterY=9 CenterZ=0 NormalX=0 NormalY=0 NormalZ=1 AngleXU=0 Radius=4
    g2: Circle CenterX=-31.25 CenterY=-9 CenterZ=0 NormalX=0 NormalY=0 NormalZ=1 AngleXU=0 Radius=4
    g3: Circle CenterX=31.25 CenterY=-9 CenterZ=0 NormalX=0 NormalY=0 NormalZ=1 AngleXU=0 Radius=4
  constraints (9):
    c: Symmetric(g0,g1,g-2)
    c: Symmetric(g2,g3,g-2)
    c: Symmetric(g3,g1,g-1)
    c: DistanceY(g3,g1) = 18
    c: DistanceX(g2,g3) = 62.5
    c: Diameter(g1) = 8
    c: Diameter(g0) = 8
    c: Diameter(g3) = 8
    c: Diameter(g2) = 8
FEATURE [PartDesign::Pocket] Pocket011  label="bolt-holes-pocket"
  BaseFeature = -> Pocket004
  Direction = (0,0,-1)
  Length = 15
  Length2 = 5
  Profile = -> Sketch048
  ReferenceAxis = -> Sketch048 [N_Axis]
  Suppressed = false
  Type = 0
FEATURE [PartDesign::Chamfer] Chamfer
  Angle = 45
  Base = -> Pocket011 [Edge350,Edge352,Edge351,Edge349]
  BaseFeature = -> Pocket011
  ChamferType = 0
  FlipDirection = false
  Size = 1
  Size2 = 1
  SupportTransform = false
  Suppressed = false
  UseAllEdges = false
FEATURE [PartDesign::Body] Body  label="deck"
  AllowCompound = false
  Group = -> [Sketch,Pad,Sketch018,Pad007,MultiTransform,Mirrored,Mirrored001,Sketch019,Pocket,Sketch020,Pocket003,Sketch021,Pocket004,Sketch048,Pocket011,Chamfer]
  Origin = -> Origin
  Placement = pos=(0,0,0) rot=(0,0,1;1.309rad)
  Tip = -> Chamfer
COMPONENT P1 — recipe-attached ("holster001", modeled in this document).
Construction recipe (the document's own serialized feature program — sketch geometry with constraints, then the solid features built on it; lengths are millimeters unless a unit is written):

FEATURE [Sketcher::SketchObject] Sketch042  label="deck-rails"
  ArcFitTolerance = 0
  AttachmentOffset = pos=(0,0,22.5) rot=(0,0,1;0rad)
  AttachmentSupport = -> [XY_Plane012]
  FullyConstrained = true
  MakeInternals = false
  MapMode = 5
  Placement = pos=(0,0,22.5) rot=(0,0,1;0rad)
  expr: Constraints[0] = Spreadsheet.railLengthNegYLong
  expr: Constraints[10] = Spreadsheet.railtruckclearance
  expr: Constraints[12] = Spreadsheet.raildiameter / 2
  expr: Constraints[14] = Spreadsheet.railLengthNegYLong
  sketch-geometry (9):
    g0: LineSegment StartX=33 StartY=-95 StartZ=0 EndX=33 EndY=42.25 EndZ=0
    g1: LineSegment [constr] StartX=-30 StartY=62.5 StartZ=0 EndX=30 EndY=62.5 EndZ=0
    g2: LineSegment [constr] StartX=30 StartY=62.5 StartZ=0 EndX=30 EndY=-62.5 EndZ=0
    g3: LineSegment [constr] StartX=30 StartY=-62.5 StartZ=0 EndX=-30 EndY=-62.5 EndZ=0
    g4: LineSegment [constr] StartX=-30 StartY=-62.5 StartZ=0 EndX=-30 EndY=62.5 EndZ=0
    g5: LineSegment StartX=-33 StartY=42.25 StartZ=0 EndX=-33 EndY=-95 EndZ=0
    g6: LineSegment StartX=-20.25 StartY=55 StartZ=0 EndX=20.25 EndY=55 EndZ=0
    g7: ArcOfCircle CenterX=-20.25 CenterY=42.25 CenterZ=0 NormalX=0 NormalY=0 NormalZ=1 AngleXU=0 Radius=12.75 StartAngle=1.5708 EndAngle=3.14159
    g8: ArcOfCircle CenterX=20.25 CenterY=42.25 CenterZ=0 NormalX=0 NormalY=0 NormalZ=1 AngleXU=0 Radius=12.75 StartAngle=6.49422e-11 EndAngle=1.5708
  constraints (24):
    c: DistanceY(g0,g-1) = 95
    c: Vertical(g0)
    c: Coincident(g1,g2)
    c: Coincident(g2,g3)
    c: Coincident(g3,g4)
    c: Coincident(g4,g1)
    c: Horizontal(g3)
    c: Vertical(g4)
    c: Symmetric(g1,g1,g-2)
    c: Symmetric(g1,g2,g-1)
    c: DistanceX(g1,g1) = 60
    c: DistanceY(g4,g4) = 125
    c: DistanceX(g2,g0) = 3
    c: Vertical(g5)
    c: DistanceY(g5,g-1) = 95
    c: Horizontal(g6)
    c: Tangent(g8,g6) = 1.5708
    c: Tangent(g8,g0) = -1.5708
    c: Tangent(g7,g6) = 1.5708
    c: Tangent(g7,g5) = -1.5708
    c: DistanceX(g5,g3) = 3
    c: Radius(g7) = 12.75
    c: Equal(g7,g8)
    c: DistanceY(g-1,g6) = 55
FEATURE [Sketcher::SketchObject] Sketch043  label="truck-rails-long"
  ArcFitTolerance = 0
  AttachmentOffset = pos=(0,0,33) rot=(0,0,1;0rad)
  AttachmentSupport = -> [YZ_Plane012]
  FullyConstrained = true
  MakeInternals = false
  MapMode = 5
  Placement = pos=(33,0,0) rot=(0.57735,0.57735,0.57735;2.0944rad)
  expr: .AttachmentOffset.Base.z = Spreadsheet.railtruckclearance / 2 + Spreadsheet.raildiameter / 2
  expr: Constraints[10] = Spreadsheet.railLengthNegYLong
  expr: Constraints[1] = Spreadsheet.railLengthPosY
  expr: Constraints[5] = Spreadsheet.raildiameter / 2
  sketch-geometry (4):
    g0: LineSegment StartX=-95 StartY=-3 StartZ=0 EndX=58 EndY=-3 EndZ=0
    g1: ArcOfCircle CenterX=-95 CenterY=9.75 CenterZ=0 NormalX=0 NormalY=0 NormalZ=1 AngleXU=0 Radius=12.75 StartAngle=1.5708 EndAngle=4.71239
    g2: LineSegment StartX=28 StartY=-19 StartZ=0 EndX=58 EndY=-19 EndZ=0
    g3: ArcOfCircle CenterX=58 CenterY=-11 CenterZ=0 NormalX=0 NormalY=0 NormalZ=1 AngleXU=0 Radius=8 StartAngle=4.71239 EndAngle=7.85398
  constraints (13):
    c: Horizontal(g0)
    c: DistanceX(g-1,g0) = 58
    c: Coincident(g1,g0)
    c: Vertical(g0,g1)
    c: Vertical(g1,g1)
    c: DistanceY(g0,g-1) = 3
    c: Horizontal(g2)
    c: Tangent(g3,g0) = 1.5708
    c: Tangent(g3,g2) = -1.5708
    c: DistanceY(g2,g0) = 16
    c: DistanceX(g1,g-1) = 95
    c: DistanceX(g-1,g2) = 28
    c: DistanceY(g0,g1) = 25.5
FEATURE [Sketcher::SketchObject] Sketch045  label="rail-profile"
  ArcFitTolerance = 0
  AttachmentSupport = -> [Sketch042]
  FullyConstrained = true
  MakeInternals = false
  MapMode = 7
  Placement = pos=(33,-95,22.5) rot=(1,0,0;1.5708rad)
  expr: Constraints[1] = Spreadsheet.raildiameter
  sketch-geometry (1):
    g0: Circle CenterX=0 CenterY=0 CenterZ=0 NormalX=0 NormalY=0 NormalZ=1 AngleXU=0 Radius=3
  constraints (2):
    c: Coincident(g0,g-1)
    c: Diameter(g0) = 6
FEATURE [Sketcher::SketchObject] Sketch070  label="rail-bend-guide"
  ArcFitTolerance = 0
  AttachmentSupport = -> [XY_Plane012]
  FullyConstrained = true
  MakeInternals = false
  MapMode = 5
  expr: Constraints[11] = Spreadsheet.railFinalSegmentsLength
  expr: Constraints[12] = Spreadsheet.railLengthNegYShort + Spreadsheet.railDeckExtension
  expr: Constraints[13] = (Spreadsheet.raildeckclearance + Spreadsheet.raildiameter) * pi * 0.5
  expr: Constraints[15] = Spreadsheet.railLengthNegYShort + Spreadsheet.railLengthPosY
  expr: Constraints[16] = (Spreadsheet.railcatchclearance + Spreadsheet.raildiameter) * pi * 0.5
  expr: Constraints[17] = Spreadsheet.railFinalSegmentsLength
  expr: Constraints[1] = (Spreadsheet.railtruckclearance + Spreadsheet.raildiameter) * pi * 0.5
  expr: Constraints[3] = Spreadsheet.railLengthNegYLong + Spreadsheet.railDeckExtension
  expr: Constraints[5] = (Spreadsheet.raildeckclearance + Spreadsheet.raildiameter) * pi * 0.5
  expr: Constraints[7] = Spreadsheet.railLengthNegYLong + Spreadsheet.railLengthPosY
  expr: Constraints[9] = (Spreadsheet.railcatchclearance + Spreadsheet.raildiameter) * pi * 0.5
  sketch-geometry (12):
    g0: GeomPoint [constr] X=-51.8363 Y=0 Z=0
    g1: GeomPoint [constr] X=51.8363 Y=0 Z=0
    g2: GeomPoint [constr] X=-191.836 Y=0 Z=0
    g3: GeomPoint [constr] X=176.836 Y=0 Z=0
    g4: GeomPoint [constr] X=-224.823 Y=0 Z=0
    g5: GeomPoint [constr] X=209.823 Y=0 Z=0
    g6: GeomPoint [constr] X=-377.823 Y=0 Z=0
    g7: GeomPoint [constr] X=347.823 Y=0 Z=0
    g8: GeomPoint [constr] X=-410.81 Y=0 Z=0
    g9: GeomPoint [constr] X=380.81 Y=0 Z=0
    g10: GeomPoint [constr] X=-530.81 Y=0 Z=0
    g11: GeomPoint [constr] X=500.81 Y=0 Z=0
  constraints (23):
    c: PointOnObject(g0,g-1)
    c: DistanceX(g0,g1) = 103.673
    c: PointOnObject(g2,g-1)
    c: DistanceX(g2,g0) = 140
    c: PointOnObject(g4,g-1)
    c: DistanceX(g4,g2) = 32.9867
    c: PointOnObject(g6,g-1)
    c: DistanceX(g6,g4) = 153
    c: PointOnObject(g8,g-1)
    c: DistanceX(g8,g6) = 32.9867
    c: PointOnObject(g10,g-1)
    c: DistanceX(g10,g8) = 120
    c: DistanceX(g1,g3) = 125
    c: DistanceX(g3,g5) = 32.9867
    c: Symmetric(g0,g1,g-2)
    c: DistanceX(g5,g7) = 138
    c: DistanceX(g7,g9) = 32.9867
    c: DistanceX(g9,g11) = 120
    c: PointOnObject(g3,g-1)
    c: PointOnObject(g5,g-1)
    c: PointOnObject(g7,g-1)
    c: PointOnObject(g9,g-1)
    c: PointOnObject(g11,g-1)
FEATURE [Sketcher::SketchObject] Sketch071  label="outline001"
  ArcFitTolerance = 0
  AttachmentSupport = -> [XY_Plane017]
  FullyConstrained = true
  MakeInternals = false
  MapMode = 5
  expr: Constraints[3] = Spreadsheet.railcatchclearance
  sketch-geometry (2):
    g0: Circle CenterX=0 CenterY=0 CenterZ=0 NormalX=0 NormalY=0 NormalZ=1 AngleXU=0 Radius=9
    g1: Circle CenterX=0 CenterY=0 CenterZ=0 NormalX=0 NormalY=0 NormalZ=1 AngleXU=0 Radius=7.5
  constraints (4):
    c: Coincident(g0,g-1)
    c: Diameter(g0) = 18
    c: Coincident(g1,g0)
    c: Diameter(g1) = 15
FEATURE [PartDesign::Pad] Pad025
  Direction = (0,0,1)
  Length = 15
  Length2 = 10
  Profile = -> Sketch071
  ReferenceAxis = -> Sketch071 [N_Axis]
  Suppressed = false
  Type = 0
FEATURE [PartDesign::Body] Body015  label="mandrel-small-rail-bend"
  AllowCompound = false
  Group = -> [Sketch071,Pad025]
  Origin = -> Origin017
  Placement = pos=(83,0,0) rot=(0,0,1;0rad)
  Tip = -> Pad025
FEATURE [Sketcher::SketchObject] Sketch072  label="outline002"
  ArcFitTolerance = 0
  AttachmentSupport = -> [XY_Plane018]
  FullyConstrained = true
  MakeInternals = false
  MapMode = 5
  expr: Constraints[3] = Spreadsheet.railtruckclearance
  sketch-geometry (2):
    g0: Circle CenterX=0 CenterY=0 CenterZ=0 NormalX=0 NormalY=0 NormalZ=1 AngleXU=0 Radius=9
    g1: Circle CenterX=0 CenterY=0 CenterZ=0 NormalX=0 NormalY=0 NormalZ=1 AngleXU=0 Radius=30
  constraints (4):
    c: Coincident(g0,g-1)
    c: Diameter(g0) = 18
    c: Coincident(g1,g0)
    c: Diameter(g1) = 60
FEATURE [PartDesign::Pad] Pad026
  Direction = (0,0,1)
  Length = 10
  Length2 = 10
  Profile = -> Sketch072
  ReferenceAxis = -> Sketch072 [N_Axis]
  Suppressed = false
  Type = 0
FEATURE [PartDesign::Body] Body016  label="mandrel-large-rail-bend"
  AllowCompound = false
  Group = -> [Sketch072,Pad026]
  Origin = -> Origin018
  Placement = pos=(92,-58,0) rot=(0,0,1;0rad)
  Tip = -> Pad026
FEATURE [Sketcher::SketchObject] Sketch083  label="truck-rails-short"
  ArcFitTolerance = 0
  AttachmentOffset = pos=(0,0,-33) rot=(0,0,1;0rad)
  AttachmentSupport = -> [YZ_Plane012]
  FullyConstrained = true
  MakeInternals = false
  MapMode = 5
  Placement = pos=(-33,0,0) rot=(0.57735,0.57735,0.57735;2.0944rad)
  expr: .AttachmentOffset.Base.z = -(Spreadsheet.railtruckclearance / 2 + Spreadsheet.raildiameter / 2)
  expr: Constraints[10] = Spreadsheet.raildiameter / 2
  expr: Constraints[11] = Spreadsheet.railLengthNegYLong
  expr: Constraints[9] = Spreadsheet.railLengthPosY
  sketch-geometry (4):
    g0: LineSegment StartX=-52 StartY=-19 StartZ=0 EndX=58 EndY=-19 EndZ=0
    g1: ArcOfCircle CenterX=58 CenterY=-11 CenterZ=0 NormalX=0 NormalY=0 NormalZ=1 AngleXU=0 Radius=8 StartAngle=4.71239 EndAngle=7.85398
    g2: LineSegment StartX=58 StartY=-3 StartZ=0 EndX=-95 EndY=-3 EndZ=0
    g3: ArcOfCircle CenterX=-95 CenterY=9.75 CenterZ=0 NormalX=0 NormalY=0 NormalZ=1 AngleXU=0 Radius=12.75 StartAngle=1.5708 EndAngle=4.71239
  constraints (15):
    c: Horizontal(g0)
    c: Coincident(g1,g0)
    c: Coincident(g2,g1)
    c: Horizontal(g2)
    c: Coincident(g3,g2)
    c: Vertical(g2,g3)
    c: Vertical(g3,g3)
    c: Vertical(g0,g1)
    c: Vertical(g1,g1)
    c: DistanceX(g-1,g1) = 58
    c: DistanceY(g1,g-1) = 3
    c: DistanceX(g3,g-1) = 95
    c: DistanceX(g0,g0) = 110
    c: DistanceY(g0,g1) = 16
    c: DistanceY(g2,g3) = 25.5
FEATURE [PartDesign::SubShapeBinder] Binder001  label="rails-shape-binder"
  BindCopyOnChange = 0
  BindMode = 0
  ClaimChildren = false
  Context = -> Part001 [Body011.Binder001.]
  Fuse = false
  MakeFace = true
  OffsetFill = false
  OffsetIntersection = false
  OffsetJoinType = 0
  OffsetOpenResult = false
  PartialLoad = false
  Relative = true
  Support = -> [Sketch042,Sketch043,Sketch083]
  _Version = 2
FEATURE [Sketcher::SketchObject] Sketch091  label="shaft-profile"
  ArcFitTolerance = 0
  AttachmentSupport = -> [YZ_Plane022]
  FullyConstrained = true
  MakeInternals = false
  MapMode = 5
  Placement = pos=(0,0,0) rot=(0.57735,0.57735,0.57735;2.0944rad)
  sketch-geometry (1):
    g0: Circle CenterX=0 CenterY=0 CenterZ=0 NormalX=0 NormalY=0 NormalZ=1 AngleXU=0 Radius=4
  constraints (2):
    c: Coincident(g0,g-1)
    c: Diameter(g0) = 8
FEATURE [PartDesign::Pad] Pad034  label="shaft-pad"
  Direction = (1,0,0)
  Length = 28
  Length2 = 10
  Placement = pos=(0,0,0) rot=(1,1,1;2.0944rad)
  Profile = -> Sketch091
  ReferenceAxis = -> Sketch091 [N_Axis]
  Suppressed = false
  Type = 0
FEATURE [Sketcher::SketchObject] Sketch092  label="head-outline"
  ArcFitTolerance = 0
  AttachmentSupport = -> [YZ_Plane022]
  FullyConstrained = true
  MakeInternals = false
  MapMode = 5
  Placement = pos=(0,0,0) rot=(0.57735,0.57735,0.57735;2.0944rad)
  sketch-geometry (1):
    g0: Circle CenterX=0 CenterY=0 CenterZ=0 NormalX=0 NormalY=0 NormalZ=1 AngleXU=0 Radius=6.5
  constraints (2):
    c: Coincident(g0,g-1)
    c: Diameter(g0) = 13
FEATURE [PartDesign::Pad] Pad035  label="head-pad"
  BaseFeature = -> Pad034
  Direction = (1,0,0)
  Length = 8
  Length2 = 10
  Placement = pos=(0,0,0) rot=(1,1,1;2.0944rad)
  Profile = -> Sketch092
  ReferenceAxis = -> Sketch092 [N_Axis]
  Suppressed = false
  Type = 0
FEATURE [Sketcher::SketchObject] Sketch093  label="hex-profile"
  ArcFitTolerance = 0
  AttachmentSupport = -> [YZ_Plane022]
  FullyConstrained = true
  MakeInternals = false
  MapMode = 5
  Placement = pos=(0,0,0) rot=(0.57735,0.57735,0.57735;2.0944rad)
  sketch-geometry (7):
    g0: LineSegment StartX=3 StartY=1.73205 StartZ=0 EndX=1.3e-15 EndY=3.4641 EndZ=0
    g1: LineSegment StartX=1.3e-15 StartY=3.4641 StartZ=0 EndX=-3 EndY=1.73205 EndZ=0
    g2: LineSegment StartX=-3 StartY=1.73205 StartZ=0 EndX=-3 EndY=-1.73205 EndZ=0
    g3: LineSegment StartX=-3 StartY=-1.73205 StartZ=0 EndX=4e-16 EndY=-3.4641 EndZ=0
    g4: LineSegment StartX=4e-16 StartY=-3.4641 StartZ=0 EndX=3 EndY=-1.73205 EndZ=0
    g5: LineSegment StartX=3 StartY=-1.73205 StartZ=0 EndX=3 EndY=1.73205 EndZ=0
    g6: Circle [constr] CenterX=0 CenterY=0 CenterZ=0 NormalX=0 NormalY=0 NormalZ=1 AngleXU=0 Radius=3.4641
  constraints (16):
    c: Coincident(g0,g1)
    c: Coincident(g1,g2)
    c: Coincident(g2,g3)
    c: Coincident(g3,g4)
    c: Coincident(g4,g5)
    c: Coincident(g5,g0)
    c: Equal(g0, g1-g5) x5
    c: PointOnObject(g0,g6)
    c: PointOnObject(g1,g6)
    c: PointOnObject(g2,g6)
    c: PointOnObject(g3,g6)
    c: PointOnObject(g4,g6)
    c: PointOnObject(g5,g6)
    c: Coincident(g6,g-1)
    c: Vertical(g5)
    c: DistanceX(g1,g0) = 6
FEATURE [PartDesign::Pocket] Pocket034  label="hex-pocket"
  BaseFeature = -> Pad035
  Direction = (-1,0,0)
  Length = 5
  Length2 = 5
  Placement = pos=(0,0,0) rot=(1,1,1;2.0944rad)
  Profile = -> Sketch093
  ReferenceAxis = -> Sketch093 [N_Axis]
  Reversed = true
  Suppressed = false
  Type = 0
FEATURE [PartDesign::Body] Body020  label="m8-bolt"
  AllowCompound = false
  Group = -> [Sketch091,Pad034,Sketch092,Pad035,Sketch093,Pocket034]
  Origin = -> Origin022
  Placement = pos=(19.6005,-17,-16.6) rot=(0,0,1;0rad)
  Tip = -> Pocket034
FEATURE [Sketcher::SketchObject] Sketch094
  ArcFitTolerance = 0
  AttachmentSupport = -> [YZ_Plane023]
  FullyConstrained = true
  MakeInternals = false
  MapMode = 5
  Placement = pos=(0,0,0) rot=(0.57735,0.57735,0.57735;2.0944rad)
  sketch-geometry (8):
    g0: LineSegment StartX=6.5 StartY=3.75278 StartZ=0 EndX=0 EndY=7.50555 EndZ=0
    g1: LineSegment StartX=0 StartY=7.50555 StartZ=0 EndX=-6.5 EndY=3.75278 EndZ=0
    g2: LineSegment StartX=-6.5 StartY=3.75278 StartZ=0 EndX=-6.5 EndY=-3.75278 EndZ=0
    g3: LineSegment StartX=-6.5 StartY=-3.75278 StartZ=0 EndX=0 EndY=-7.50555 EndZ=0
    g4: LineSegment StartX=0 StartY=-7.50555 StartZ=0 EndX=6.5 EndY=-3.75278 EndZ=0
    g5: LineSegment StartX=6.5 StartY=-3.75278 StartZ=0 EndX=6.5 EndY=3.75278 EndZ=0
    g6: Circle [constr] CenterX=0 CenterY=0 CenterZ=0 NormalX=0 NormalY=0 NormalZ=1 AngleXU=0 Radius=7.50555
    g7: Circle CenterX=0 CenterY=0 CenterZ=0 NormalX=0 NormalY=0 NormalZ=1 AngleXU=0 Radius=3.5
  constraints (18):
    c: Coincident(g0,g1)
    c: Coincident(g1,g2)
    c: Coincident(g2,g3)
    c: Coincident(g3,g4)
    c: Coincident(g4,g5)
    c: Coincident(g5,g0)
    c: Equal(g0, g1-g5) x5
    c: PointOnObject(g0,g6)
    c: PointOnObject(g1,g6)
    c: PointOnObject(g2,g6)
    c: PointOnObject(g3,g6)
    c: PointOnObject(g4,g6)
    c: PointOnObject(g5,g6)
    c: Coincident(g6,g-1)
    c: Vertical(g5)
    c: DistanceX(g1,g0) = 13
    c: Coincident(g7,g6)
    c: Diameter(g7) = 7
FEATURE [PartDesign::Pad] Pad036
  Direction = (1,0,0)
  Length = 6
  Length2 = 10
  Placement = pos=(0,0,0) rot=(1,1,1;2.0944rad)
  Profile = -> Sketch094
  ReferenceAxis = -> Sketch094 [N_Axis]
  Suppressed = false
  Type = 0
FEATURE [PartDesign::Body] Body021  label="m8-nut"
  AllowCompound = false
  Group = -> [Sketch094,Pad036]
  Origin = -> Origin023
  Placement = pos=(38,-17,-16.6) rot=(0,-1,0;0rad)
  Tip = -> Pad036
FEATURE [Sketcher::SketchObject] Sketch095
  ArcFitTolerance = 0
  AttachmentOffset = pos=(0,0,66) rot=(0,0,1;0rad)
  AttachmentSupport = -> [XZ_Plane024]
  FullyConstrained = false
  MakeInternals = false
  MapMode = 5
  Placement = pos=(0,-66,1.47e-14) rot=(1,0,0;1.5708rad)
  sketch-geometry (13):
    g0: LineSegment StartX=8 StartY=17.8681 StartZ=0 EndX=-3.5 EndY=17.8681 EndZ=0
    g1: ArcOfCircle CenterX=-3.5 CenterY=15.8681 CenterZ=0 NormalX=0 NormalY=0 NormalZ=1 AngleXU=0 Radius=2 StartAngle=1.5708 EndAngle=3.14159
    g2: GeomPoint [constr] X=-5.5 Y=17.8681 Z=0
    g3: ArcOfCircle CenterX=8 CenterY=15.8681 CenterZ=0 NormalX=0 NormalY=0 NormalZ=1 AngleXU=0 Radius=2 StartAngle=0 EndAngle=1.5708
    g4: GeomPoint [constr] X=10 Y=17.8681 Z=0
    g5: GeomPoint [constr] X=10 Y=-5 Z=0
    g6: LineSegment StartX=-5.5 StartY=15.8681 StartZ=0 EndX=-5.5 EndY=-6 EndZ=0
    g7: LineSegment StartX=-3.5 StartY=-8 StartZ=0 EndX=8 EndY=-8 EndZ=0
    g8: LineSegment StartX=10 StartY=-6 StartZ=0 EndX=10 EndY=15.8681 EndZ=0
    g9: ArcOfCircle CenterX=-3.5 CenterY=-6 CenterZ=0 NormalX=0 NormalY=0 NormalZ=1 AngleXU=0 Radius=2 StartAngle=3.14159 EndAngle=4.71239
    g10: GeomPoint [constr] X=-5.5 Y=-8 Z=0
    g11: ArcOfCircle CenterX=8 CenterY=-6 CenterZ=0 NormalX=0 NormalY=0 NormalZ=1 AngleXU=0 Radius=2 StartAngle=4.71239 EndAngle=6.28319
    g12: GeomPoint [constr] X=10 Y=-8 Z=0
  constraints (26):
    c: Horizontal(g0)
    c: PointOnObject(g2,g0)
    c: Tangent(g0,g1) = -1.5708
    c: PointOnObject(g4,g0)
    c: Tangent(g0,g3) = -1.5708
    c: Radius(g1) = 2
    c: Radius(g3) = 2
    c: Vertical(g6)
    c: Horizontal(g7)
    c: Vertical(g8)
    c: DistanceX(g10,g-1) = 5.5
    c: PointOnObject(g10,g6)
    c: PointOnObject(g10,g7)
    c: Tangent(g6,g9) = -1.5708
    c: Tangent(g7,g9) = -1.5708
    c: PointOnObject(g12,g7)
    c: PointOnObject(g12,g8)
    c: Tangent(g7,g11) = -1.5708
    c: Tangent(g8,g11) = -1.5708
    c: Radius(g9) = 2
    c: Radius(g11) = 2
    c: DistanceY(g10,g-1) = 8
    c: Tangent(g8,g3) = -1.5708
    c: DistanceX(g-1,g12) = 10
    c: Vertical(g2,g1)
    c: Tangent(g1,g6) = -1.5708
FEATURE [PartDesign::Pad] Pad037
  Direction = (0,-1,2e-16)
  Length = 65
  Length2 = 10
  Placement = pos=(0,0,0) rot=(1,0,0;1.5708rad)
  Profile = -> Sketch095
  ReferenceAxis = -> Sketch095 [N_Axis]
  Reversed = true
  Suppressed = false
  Type = 0
FEATURE [Sketcher::SketchObject] Sketch096  label="ramp-outline"
  ArcFitTolerance = 0
  AttachmentOffset = pos=(0,0,1) rot=(0,0,1;0rad)
  AttachmentSupport = -> [XY_Plane024]
  FullyConstrained = false
  MakeInternals = false
  MapMode = 5
  Placement = pos=(0,0,1) rot=(0,0,1;0rad)
  sketch-geometry (3):
    g0: LineSegment StartX=-4.84971 StartY=-30.2537 StartZ=0 EndX=-4.84971 EndY=-1.1201 EndZ=0
    g1: LineSegment StartX=-13.4497 StartY=-30.2537 StartZ=0 EndX=-4.84971 EndY=-1.1201 EndZ=0
    g2: LineSegment StartX=-13.4497 StartY=-30.2537 StartZ=0 EndX=-4.84971 EndY=-30.2537 EndZ=0
  constraints (5):
    c: Vertical(g0)
    c: Coincident(g1,g0)
    c: Horizontal(g2)
    c: Coincident(g0,g2)
    c: Coincident(g1,g2)
FEATURE [PartDesign::Pad] Pad038  label="ramp-pad"
  BaseFeature = -> Pad037
  Direction = (0,0,1)
  Length = 13
  Length2 = 7
  Placement = pos=(0,0,0) rot=(1,0,0;1.5708rad)
  Profile = -> Sketch096
  ReferenceAxis = -> Sketch096 [N_Axis]
  Suppressed = false
  Type = 0
FEATURE [Sketcher::SketchObject] Sketch098  label="bolt-hole-outline"
  ArcFitTolerance = 0
  AttachmentOffset = pos=(-37,7.42,0) rot=(0,0,1;0rad)
  AttachmentSupport = -> [YZ_Plane024]
  FullyConstrained = true
  MakeInternals = false
  MapMode = 5
  Placement = pos=(0,-37,7.42) rot=(0.57735,0.57735,0.57735;2.0944rad)
  sketch-geometry (1):
    g0: Circle CenterX=0 CenterY=0 CenterZ=0 NormalX=0 NormalY=0 NormalZ=1 AngleXU=0 Radius=4
  constraints (2):
    c: Diameter(g0) = 8
    c: Coincident(g0,g-1)
FEATURE [PartDesign::Pocket] Pocket036  label="bolt-hole-pocket"
  BaseFeature = -> Pad038
  Direction = (-1,0,0)
  Length = 65
  Length2 = 5
  Midplane = true
  Placement = pos=(0,0,0) rot=(1,0,0;1.5708rad)
  Profile = -> Sketch098
  ReferenceAxis = -> Sketch098 [N_Axis]
  Suppressed = false
  Type = 0
FEATURE [Sketcher::SketchObject] Sketch099
  ArcFitTolerance = 0
  AttachmentOffset = pos=(0,0,1) rot=(0,0,1;0rad)
  AttachmentSupport = -> [XZ_Plane024]
  FullyConstrained = true
  MakeInternals = false
  MapMode = 5
  Placement = pos=(0,-1,2e-16) rot=(1,0,0;1.5708rad)
  expr: Constraints[1] = Spreadsheet.raildiameter + 0.3 mm
  sketch-geometry (1):
    g0: Circle CenterX=0 CenterY=0 CenterZ=0 NormalX=0 NormalY=0 NormalZ=1 AngleXU=0 Radius=3.15
  constraints (2):
    c: Coincident(g0,g-1)
    c: Diameter(g0) = 6.3
FEATURE [PartDesign::Pocket] Pocket037
  BaseFeature = -> Pocket036
  Direction = (0,1,-2e-16)
  Length = 75
  Length2 = 5
  Placement = pos=(0,0,0) rot=(1,0,0;1.5708rad)
  Profile = -> Sketch099
  ReferenceAxis = -> Sketch099 [N_Axis]
  Reversed = true
  Suppressed = false
  Type = 0
FEATURE [Sketcher::SketchObject] Sketch100
  ArcFitTolerance = 0
  AttachmentOffset = pos=(0,0,1) rot=(0,0,1;0rad)
  AttachmentSupport = -> [XZ_Plane024]
  FullyConstrained = false
  MakeInternals = false
  MapMode = 5
  Placement = pos=(0,-1,2e-16) rot=(1,0,0;1.5708rad)
  sketch-geometry (6):
    g0: LineSegment StartX=-6.32089 StartY=20 StartZ=0 EndX=1.01752 EndY=20 EndZ=0
    g1: LineSegment StartX=1.01752 StartY=20 StartZ=0 EndX=1.01752 EndY=0 EndZ=0
    g2: LineSegment StartX=1.01752 StartY=0 StartZ=0 EndX=0.034595 EndY=0 EndZ=0
    g3: LineSegment StartX=0.034595 StartY=0 StartZ=0 EndX=0.034595 EndY=16.4036 EndZ=0
    g4: LineSegment StartX=0.034595 StartY=16.4036 StartZ=0 EndX=-6.32089 EndY=16.4036 EndZ=0
    g5: LineSegment StartX=-6.32089 StartY=16.4036 StartZ=0 EndX=-6.32089 EndY=20 EndZ=0
  constraints (14):
    c: Coincident(g0,g1)
    c: Coincident(g1,g2)
    c: Horizontal(g2)
    c: Vertical(g1)
    c: PointOnObject(g2,g-1)
    c: DistanceY(g2,g0) = 20
    c: Coincident(g3,g2)
    c: Vertical(g3)
    c: Coincident(g4,g3)
    c: Horizontal(g4)
    c: Coincident(g5,g4)
    c: Vertical(g5)
    c: Coincident(g0,g5)
    c: Horizontal(g0)
FEATURE [PartDesign::Pocket] Pocket038
  BaseFeature = -> Pocket037
  Direction = (0,1,-2e-16)
  Length = 65
  Length2 = 5
  Placement = pos=(0,0,0) rot=(1,0,0;1.5708rad)
  Profile = -> Sketch100
  ReferenceAxis = -> Sketch100 [N_Axis]
  Reversed = true
  Suppressed = false
  Type = 0
FEATURE [Sketcher::SketchObject] Sketch102  label="hex-nut-hole-outline"
  ArcFitTolerance = 1e-06
  AttachmentOffset = pos=(-37,7.42,10) rot=(0,0,1;0rad)
  AttachmentSupport = -> [YZ_Plane024]
  FullyConstrained = true
  MakeInternals = false
  MapMode = 5
  Placement = pos=(10,-37,7.42) rot=(0.57735,0.57735,0.57735;2.0944rad)
  sketch-geometry (7):
    g0: LineSegment StartX=0 StartY=7.62102 StartZ=0 EndX=-6.6 EndY=3.81051 EndZ=0
    g1: LineSegment StartX=-6.6 StartY=3.81051 StartZ=0 EndX=-6.6 EndY=-3.81051 EndZ=0
    g2: LineSegment StartX=-6.6 StartY=-3.81051 StartZ=0 EndX=-8e-15 EndY=-7.62102 EndZ=0
    g3: LineSegment StartX=-8e-15 StartY=-7.62102 StartZ=0 EndX=6.6 EndY=-3.81051 EndZ=0
    g4: LineSegment StartX=6.6 StartY=-3.81051 StartZ=0 EndX=6.6 EndY=3.81051 EndZ=0
    g5: LineSegment StartX=6.6 StartY=3.81051 StartZ=0 EndX=0 EndY=7.62102 EndZ=0
    g6: Circle [constr] CenterX=0 CenterY=0 CenterZ=0 NormalX=0 NormalY=0 NormalZ=1 AngleXU=0 Radius=7.62102
  constraints (16):
    c: Coincident(g0,g1)
    c: Coincident(g1,g2)
    c: Coincident(g2,g3)
    c: Coincident(g3,g4)
    c: Coincident(g4,g5)
    c: Coincident(g5,g0)
    c: Equal(g0, g1-g5) x5
    c: PointOnObject(g0,g6)
    c: PointOnObject(g1,g6)
    c: PointOnObject(g2,g6)
    c: PointOnObject(g3,g6)
    c: PointOnObject(g4,g6)
    c: PointOnObject(g5,g6)
    c: Coincident(g6,g-1)
    c: PointOnObject(g0,g-2)
    c: DistanceX(g1,g3) = 13.2
FEATURE [Sketcher::SketchObject] Sketch103
  ArcFitTolerance = 1e-06
  AttachmentOffset = pos=(0,0,-8) rot=(0,0,1;0rad)
  AttachmentSupport = -> [XY_Plane024]
  FullyConstrained = false
  MakeInternals = false
  MapMode = 5
  Placement = pos=(0,0,-8) rot=(0,0,1;0rad)
  sketch-geometry (10):
    g0: LineSegment StartX=6.49059 StartY=-32.6161 StartZ=0 EndX=6.49059 EndY=-66 EndZ=0
    g1: LineSegment StartX=6.49059 StartY=-66 StartZ=0 EndX=18.8419 EndY=-66 EndZ=0
    g2: LineSegment StartX=33.5251 StartY=-54.067 StartZ=0 EndX=39.0082 EndY=-27.8163 EndZ=0
    g3: LineSegment StartX=29.2377 StartY=-25.6881 StartZ=0 EndX=24.8143 EndY=-45.1928 EndZ=0
    g4: ArcOfCircle CenterX=17.5 CenterY=-43.534 CenterZ=0 NormalX=0 NormalY=0 NormalZ=1 AngleXU=0 Radius=7.5 StartAngle=3.14159 EndAngle=6.06017
    g5: ArcOfCircle CenterX=18.8419 CenterY=-51 CenterZ=0 NormalX=0 NormalY=0 NormalZ=1 AngleXU=0 Radius=15 StartAngle=4.71239 EndAngle=6.07727
    g6: GeomPoint [constr] X=31.0325 Y=-66 Z=0
    g7: ArcOfCircle CenterX=34.1138 CenterY=-26.794 CenterZ=0 NormalX=0 NormalY=0 NormalZ=1 AngleXU=0 Radius=5 StartAngle=6.07727 EndAngle=9.20176
    g8: LineSegment StartX=10 StartY=-43.534 StartZ=0 EndX=10 EndY=-32.6161 EndZ=0
    g9: LineSegment StartX=6.49059 StartY=-32.6161 StartZ=0 EndX=10 EndY=-32.6161 EndZ=0
  constraints (21):
    c: Coincident(g1,g0)
    c: Horizontal(g1)
    c: Diameter(g4) = 15
    c: PointOnObject(g6,g1)
    c: PointOnObject(g6,g2)
    c: Tangent(g1,g5) = -1.5708
    c: Tangent(g2,g5) = -1.5708
    c: Radius(g5) = 15
    c: Tangent(g7,g3) = -1.5708
    c: Tangent(g7,g2) = -1.5708
    c: Distance(g3,g3) = 20
    c: Diameter(g7) = 10
    c: Tangent(g3,g4) = 1.5708
    c: Vertical(g8)
    c: Coincident(g9,g0)
    c: Coincident(g9,g8)
    c: Horizontal(g9)
    c: Tangent(g8,g4) = 1.5708
    c: DistanceX(g-1,g8) = 10
    c: Vertical(g0)
    c: DistanceY(g0,g-1) = 66
FEATURE [PartDesign::Pad] Pad040
  BaseFeature = -> Pocket038
  Direction = (0,0,1)
  Length = 18
  Length2 = 10
  Placement = pos=(0,0,0) rot=(1,0,0;1.5708rad)
  Profile = -> Sketch103
  ReferenceAxis = -> Sketch103 [N_Axis]
  Refine = true
  Suppressed = false
  Type = 0
FEATURE [PartDesign::Pocket] Pocket039  label="hex-nut-pocket"
  BaseFeature = -> Pad040
  Direction = (-1,0,0)
  Length = 6
  Length2 = 5
  Placement = pos=(0,0,0) rot=(1,0,0;1.5708rad)
  Profile = -> Sketch102
  ReferenceAxis = -> Sketch102 [N_Axis]
  Refine = true
  Suppressed = false
  Type = 0
FEATURE [PartDesign::Body] Body022  label="catch"
  AllowCompound = false
  Group = -> [Sketch095,Pad037,Sketch096,Pad038,Sketch098,Pocket036,Sketch099,Pocket037,Sketch100,Pocket038,Sketch102,Sketch103,Pad040,Pocket039]
  Origin = -> Origin024
  Placement = pos=(33,20,-24) rot=(0,0,1;0rad)
  Tip = -> Pocket039
FEATURE [Sketcher::SketchObject] Sketch113
  ArcFitTolerance = 1e-06
  AttachmentOffset = pos=(0,0,28) rot=(0,0,1;0rad)
  AttachmentSupport = -> [XZ_Plane032]
  FullyConstrained = true
  MakeInternals = false
  MapMode = 5
  Placement = pos=(0,-28,6.2e-15) rot=(1,0,0;1.5708rad)
  sketch-geometry (16):
    g0: LineSegment StartX=-39 StartY=2.5 StartZ=0 EndX=39 EndY=2.5 EndZ=0
    g1: LineSegment StartX=-39 StartY=2.5 StartZ=0 EndX=-39 EndY=0 EndZ=0
    g2: LineSegment StartX=-37 StartY=0 StartZ=0 EndX=-37 EndY=1.5 EndZ=0
    g3: LineSegment StartX=-37 StartY=1.5 StartZ=0 EndX=-1 EndY=1.5 EndZ=0
    g4: GeomPoint X=-38 Y=0 Z=0
    g5: LineSegment StartX=-39 StartY=0 StartZ=0 EndX=-38 EndY=0 EndZ=0
    g6: LineSegment StartX=-37 StartY=0 StartZ=0 EndX=-38 EndY=0 EndZ=0
    g7: LineSegment StartX=-1 StartY=1.5 StartZ=0 EndX=-1 EndY=0 EndZ=0
    g8: LineSegment StartX=-1 StartY=0 StartZ=0 EndX=0 EndY=0 EndZ=0
    g9: LineSegment StartX=0 StartY=0 StartZ=0 EndX=1 EndY=0 EndZ=0
    g10: LineSegment StartX=1 StartY=0 StartZ=0 EndX=1 EndY=1.5 EndZ=0
    g11: LineSegment StartX=1 StartY=1.5 StartZ=0 EndX=37 EndY=1.5 EndZ=0
    g12: LineSegment StartX=37 StartY=1.5 StartZ=0 EndX=37 EndY=0 EndZ=0
    g13: LineSegment StartX=39 StartY=0 StartZ=0 EndX=39 EndY=2.5 EndZ=0
    g14: LineSegment StartX=37 StartY=0 StartZ=0 EndX=38 EndY=0 EndZ=0
    g15: LineSegment StartX=38 StartY=0 StartZ=0 EndX=39 EndY=0 EndZ=0
  constraints (46):
    c: Horizontal(g0)
    c: Coincident(g1,g0)
    c: Vertical(g1)
    c: Vertical(g2)
    c: Coincident(g3,g2)
    c: Horizontal(g3)
    c: Coincident(g5,g1)
    c: Coincident(g5,g4)
    c: Horizontal(g5)
    c: Coincident(g6,g2)
    c: Coincident(g6,g4)
    c: Horizontal(g6)
    c: Equal(g5,g6)
    c: DistanceX(g1,g2) = 2
    c: Coincident(g7,g3)
    c: Vertical(g7)
    c: Coincident(g8,g7)
    c: Horizontal(g8)
    c: Coincident(g9,g8)
    c: Horizontal(g9)
    c: Coincident(g10,g9)
    c: Vertical(g10)
    c: Equal(g8,g9)
    c: DistanceX(g4,g8) = 38
    c: DistanceX(g7,g9) = 2
    c: Coincident(g11,g10)
    c: Horizontal(g11)
    c: Coincident(g12,g11)
    c: Vertical(g12)
    c: Vertical(g13)
    c: Coincident(g0,g13)
    c: DistanceX(g12,g13) = 2
    c: Horizontal(g3,g10)
    c: DistanceY(g1,g1) = 2.5
    c: Distance(g3,g0) = 1
    c: PointOnObject(g1,g-1)
    c: PointOnObject(g7,g-1)
    c: PointOnObject(g12,g-1)
    c: PointOnObject(g8,g-2)
    c: Coincident(g14,g12)
    c: PointOnObject(g14,g-1)
    c: Coincident(g15,g14)
    c: Coincident(g15,g13)
    c: Horizontal(g15)
    c: Equal(g15,g14)
    c: DistanceX(g8,g14) = 38
FEATURE [Sketcher::SketchObject] Sketch114
  ArcFitTolerance = 1e-06
  AttachmentSupport = -> [XY_Plane032]
  FullyConstrained = true
  MakeInternals = false
  MapMode = 5
  sketch-geometry (10):
    g0: LineSegment StartX=-42 StartY=147 StartZ=0 EndX=-42 EndY=-27 EndZ=0
    g1: LineSegment StartX=-36 StartY=-33 StartZ=0 EndX=36 EndY=-33 EndZ=0
    g2: LineSegment StartX=42 StartY=-27 StartZ=0 EndX=42 EndY=147 EndZ=0
    g3: LineSegment StartX=36 StartY=153 StartZ=0 EndX=-36 EndY=153 EndZ=0
    g4: ArcOfCircle CenterX=-36 CenterY=147 CenterZ=0 NormalX=0 NormalY=0 NormalZ=1 AngleXU=0 Radius=6 StartAngle=1.5708 EndAngle=3.14159
    g5: ArcOfCircle CenterX=-36 CenterY=-27 CenterZ=0 NormalX=0 NormalY=0 NormalZ=1 AngleXU=0 Radius=6 StartAngle=3.14159 EndAngle=4.71239
    g6: ArcOfCircle CenterX=36 CenterY=-27 CenterZ=0 NormalX=0 NormalY=0 NormalZ=1 AngleXU=0 Radius=6 StartAngle=4.71239 EndAngle=6.28319
    g7: ArcOfCircle CenterX=36 CenterY=147 CenterZ=0 NormalX=0 NormalY=0 NormalZ=1 AngleXU=0 Radius=6 StartAngle=1.8e-15 EndAngle=1.5708
    g8: GeomPoint [constr] X=-42 Y=153 Z=0
    g9: GeomPoint [constr] X=42 Y=-33 Z=0
  constraints (23):
    c: Tangent(g0,g4) = -1.5708
    c: Tangent(g0,g5) = -1.5708
    c: Tangent(g1,g5) = -1.5708
    c: Tangent(g1,g6) = -1.5708
    c: Tangent(g2,g6) = -1.5708
    c: Tangent(g2,g7) = -1.5708
    c: Tangent(g3,g7) = -1.5708
    c: Tangent(g3,g4) = -1.5708
    c: Vertical(g0)
    c: Vertical(g2)
    c: Horizontal(g1)
    c: Horizontal(g3)
    c: Equal(g4,g5)
    c: Equal(g5,g6)
    c: PointOnObject(g8,g0)
    c: PointOnObject(g8,g3)
    c: PointOnObject(g9,g1)
    c: PointOnObject(g9,g2)
    c: Symmetric(g0,g2,g-2)
    c: DistanceX(g0,g2) = 84
    c: Radius(g5) = 6
    c: DistanceY(g1,g-1) = 33
    c: Distance(g3,g-1) = 153
FEATURE [PartDesign::Pad] Pad044
  Direction = (0,0,1)
  Length = 1
  Length2 = 10
  Profile = -> Sketch114
  ReferenceAxis = -> Sketch114 [N_Axis]
  Refine = true
  Suppressed = false
  Type = 0
FEATURE [PartDesign::Pad] Pad043
  BaseFeature = -> Pad044
  Direction = (0,-1,2e-16)
  Length = 25
  Length2 = 10
  Profile = -> Sketch113
  ReferenceAxis = -> Sketch113 [N_Axis]
  Refine = true
  Reversed = true
  Suppressed = false
  Type = 0
FEATURE [PartDesign::LinearPattern] LinearPattern
  BaseFeature = -> Pad043
  Direction = -> Y_Axis032
  Length = 150
  Mode = 1
  Occurrences = 4
  Offset = 50
  Originals = -> [Pad043]
  Refine = true
  Suppressed = false
  TransformMode = 0
FEATURE [PartDesign::Body] Body028  label="MOLLE-base"
  AllowCompound = false
  Group = -> [Pad044,Sketch114,Sketch113,Pad043,LinearPattern]
  Origin = -> Origin032
  Placement = pos=(3.7e-15,-59,31) rot=(0,1,0;3.14159rad)
  Tip = -> LinearPattern
FEATURE [Sketcher::SketchObject] Sketch115
  ArcFitTolerance = 1e-06
  AttachmentSupport = -> [XY_Plane033]
  FullyConstrained = true
  MakeInternals = false
  MapMode = 5
  sketch-geometry (12):
    g0: LineSegment StartX=-12.5 StartY=-117 StartZ=0 EndX=12.5 EndY=-117 EndZ=0
    g1: LineSegment StartX=7 StartY=0 StartZ=0 EndX=-7 EndY=0 EndZ=0
    g2: Circle CenterX=0 CenterY=-25 CenterZ=0 NormalX=0 NormalY=0 NormalZ=1 AngleXU=0 Radius=2.5
    g3: Circle CenterX=0 CenterY=-44.5 CenterZ=0 NormalX=0 NormalY=0 NormalZ=1 AngleXU=0 Radius=2.5
    g4: Circle CenterX=0 CenterY=-64 CenterZ=0 NormalX=0 NormalY=0 NormalZ=1 AngleXU=0 Radius=2.5
    g5: Circle CenterX=0 CenterY=-83.5 CenterZ=0 NormalX=0 NormalY=0 NormalZ=1 AngleXU=0 Radius=2.5
    g6: LineSegment StartX=-12.5 StartY=-117 StartZ=0 EndX=-12.5 EndY=-5 EndZ=0
    g7: LineSegment StartX=12.5 StartY=-117 StartZ=0 EndX=12.5 EndY=-5 EndZ=0
    g8: LineSegment StartX=-12.5 StartY=-5 StartZ=0 EndX=-7 EndY=-5 EndZ=0
    g9: LineSegment StartX=-7 StartY=-5 StartZ=0 EndX=-7 EndY=0 EndZ=0
    g10: LineSegment StartX=12.5 StartY=-5 StartZ=0 EndX=7 EndY=-5 EndZ=0
    g11: LineSegment StartX=7 StartY=-5 StartZ=0 EndX=7 EndY=0 EndZ=0
  constraints (34):
    c: Symmetric(g1,g1,g-2)
    c: PointOnObject(g1,g-1)
    c: DistanceY(g0,g1) = 117
    c: PointOnObject(g2,g-2)
    c: Diameter(g2) = 5
    c: PointOnObject(g3,g-2)
    c: PointOnObject(g4,g-2)
    c: PointOnObject(g5,g-2)
    c: Equal(g3,g2)
    c: Equal(g2,g4)
    c: Equal(g2,g5)
    c: DistanceY(g3,g2) = 19.5
    c: DistanceY(g4,g3) = 19.5
    c: DistanceY(g5,g4) = 19.5
    c: DistanceX(g0,g0) = 25
    c: Coincident(g6,g0)
    c: Vertical(g6)
    c: Coincident(g7,g0)
    c: Vertical(g7)
    c: DistanceX(g1,g1) = 14
    c: Coincident(g8,g6)
    c: Horizontal(g8)
    c: Coincident(g9,g8)
    c: Coincident(g9,g1)
    c: Vertical(g9)
    c: Coincident(g10,g7)
    c: Horizontal(g10)
    c: Coincident(g11,g10)
    c: Coincident(g11,g1)
    c: Vertical(g11)
    c: Symmetric(g0,g0,g-2)
    c: Horizontal(g8,g10)
    c: DistanceY(g9,g9) = 5
    c: DistanceY(g2,g-1) = 25
FEATURE [PartDesign::Pad] Pad045
  Direction = (0,0,1)
  Length = 8
  Length2 = 10
  Profile = -> Sketch115
  ReferenceAxis = -> Sketch115 [N_Axis]
  Refine = true
  Suppressed = false
  Type = 0
FEATURE [Sketcher::SketchObject] Sketch125  label="catch-rail"
  ArcFitTolerance = 1e-06
  AttachmentOffset = pos=(0,0,-19) rot=(0,0,1;0rad)
  AttachmentSupport = -> [XY_Plane012]
  FullyConstrained = true
  MakeInternals = false
  MapMode = 5
  Placement = pos=(0,0,-19) rot=(0,0,1;0rad)
  sketch-geometry (6):
    g0: LineSegment StartX=32.3227 StartY=24.7785 StartZ=0 EndX=18 EndY=-7.77854 EndZ=0
    g1: ArcOfCircle CenterX=25 CenterY=28 CenterZ=0 NormalX=0 NormalY=0 NormalZ=1 AngleXU=0 Radius=8 StartAngle=5.86874 EndAngle=6.28319
    g2: LineSegment StartX=25.3227 StartY=-19 StartZ=0 EndX=37.3227 EndY=-19 EndZ=0
    g3: ArcOfCircle CenterX=25.3227 CenterY=-11 CenterZ=0 NormalX=0 NormalY=0 NormalZ=1 AngleXU=0 Radius=8 StartAngle=2.72715 EndAngle=4.71239
    g4: LineSegment StartX=43.4511 StartY=-16.1423 StartZ=0 EndX=59.5208 EndY=3.00881 EndZ=0
    g5: ArcOfCircle CenterX=37.3227 CenterY=-11 CenterZ=0 NormalX=0 NormalY=0 NormalZ=1 AngleXU=0 Radius=8 StartAngle=4.71239 EndAngle=5.58505
  constraints (17):
    c: Tangent(g1,g0) = 1.5708
    c: DistanceY(g-1,g1) = 28
    c: Radius(g1) = 8
    c: Horizontal(g2)
    c: Tangent(g3,g0) = -1.5708
    c: Tangent(g3,g2) = -1.5708
    c: Radius(g3) = 8
    c: Radius(g5) = 8
    c: Tangent(g5,g2) = -1.5708
    c: Tangent(g5,g4) = -1.5708
    c: Horizontal(g1,g1)
    c: DistanceX(g-1,g1) = 33
    c: DistanceY(g2,g-1) = 19
    c: DistanceX(g-1,g0) = 18
    c: DistanceX(g2,g2) = 12
    c: Angle(g4,g2) = 2.26893
    c: Distance(g4,g4) = 25
FEATURE [PartDesign::SubShapeBinder] Binder  label="rails-shape-binder-2"
  BindCopyOnChange = 0
  BindMode = 0
  ClaimChildren = false
  Context = -> Part001 [Body011.Binder.]
  Fuse = false
  MakeFace = true
  OffsetFill = false
  OffsetIntersection = false
  OffsetJoinType = 0
  OffsetOpenResult = false
  PartialLoad = false
  Refine = true
  Relative = true
  Support = -> [Sketch125,Sketch042,Sketch043,Sketch083]
  _Version = 2
FEATURE [Sketcher::SketchObject] Sketch126  label="wheel-cap-rail"
  ArcFitTolerance = 1e-06
  AttachmentOffset = pos=(0,0,-19) rot=(0,0,1;0rad)
  AttachmentSupport = -> [XY_Plane012]
  FullyConstrained = true
  MakeInternals = false
  MapMode = 5
  Placement = pos=(0,0,-19) rot=(0,0,1;0rad)
  sketch-geometry (1):
    g0: ArcOfCircle CenterX=0 CenterY=-52 CenterZ=0 NormalX=0 NormalY=0 NormalZ=1 AngleXU=0 Radius=33 StartAngle=3.14159 EndAngle=6.28319
  constraints (5):
    c: PointOnObject(g0,g-2)
    c: Horizontal(g0,g0)
    c: Radius(g0) = 33
    c: Horizontal(g0,g0)
    c: DistanceY(g0,g-1) = 52
FEATURE [PartDesign::SubShapeBinder] Binder002  label="rails-shape-binder-3"
  BindCopyOnChange = 0
  BindMode = 0
  ClaimChildren = false
  Context = -> Part001 [Body011.Binder002.]
  Fuse = false
  MakeFace = true
  OffsetFill = false
  OffsetIntersection = false
  OffsetJoinType = 0
  OffsetOpenResult = false
  PartialLoad = false
  Refine = true
  Relative = true
  Support = -> [Sketch125,Sketch042,Sketch043,Sketch083,Sketch126]
  _Version = 2
FEATURE [PartDesign::AdditivePipe] AdditivePipe
  AuxilleryCurvelinear = true
  AuxillerySpineTangent = false
  Binormal = (0,0,0)
  Mode = 0
  Placement = pos=(0,0,22.5) rot=(0,0,1;0rad)
  Profile = -> Sketch045
  Spine = -> Binder002
  SpineTangent = false
  Suppressed = false
  Transformation = 0
  Transition = 0
FEATURE [PartDesign::Body] Body011  label="rails"
  AllowCompound = false
  Group = -> [Sketch042,Sketch043,Sketch045,AdditivePipe,Sketch070,Sketch083,Binder001,Sketch125,Binder,Sketch126,Binder002]
  Origin = -> Origin012
  Tip = -> AdditivePipe
FEATURE [Sketcher::SketchObject] Sketch134
  ArcFitTolerance = 1e-06
  AttachmentSupport = -> [YZ_Plane033]
  FullyConstrained = false
  MakeInternals = false
  MapMode = 5
  Placement = pos=(0,0,0) rot=(0.57735,0.57735,0.57735;2.0944rad)
  sketch-geometry (12):
    g0: LineSegment StartX=-112 StartY=0 StartZ=0 EndX=-117 EndY=2 EndZ=0
    g1: LineSegment StartX=-117 StartY=2 StartZ=0 EndX=-117 EndY=6 EndZ=0
    g2: LineSegment StartX=-117 StartY=6 StartZ=0 EndX=-112 EndY=8 EndZ=0
    g3: LineSegment StartX=-112 StartY=8 StartZ=0 EndX=-93 EndY=8 EndZ=0
    g4: LineSegment StartX=-93 StartY=8 StartZ=0 EndX=-89 EndY=4 EndZ=0
    g5: LineSegment StartX=-89 StartY=4 StartZ=0 EndX=0 EndY=4 EndZ=0
    g6: LineSegment StartX=0 StartY=4 StartZ=0 EndX=0 EndY=0 EndZ=0
    g7: LineSegment StartX=0 StartY=0 StartZ=0 EndX=-112 EndY=0 EndZ=0
    g8: LineSegment StartX=-143.62 StartY=27.2064 StartZ=0 EndX=-143.62 EndY=-17.1049 EndZ=0
    g9: LineSegment StartX=-143.62 StartY=-17.1049 StartZ=0 EndX=13.7462 EndY=-17.1049 EndZ=0
    g10: LineSegment StartX=13.7462 StartY=-17.1049 StartZ=0 EndX=13.7462 EndY=27.2064 EndZ=0
    g11: LineSegment StartX=13.7462 StartY=27.2064 StartZ=0 EndX=-143.62 EndY=27.2064 EndZ=0
  constraints (31):
    c: PointOnObject(g0,g-1)
    c: Coincident(g1,g0)
    c: Vertical(g1)
    c: Coincident(g2,g1)
    c: Coincident(g3,g2)
    c: Horizontal(g3)
    c: Coincident(g4,g3)
    c: Coincident(g5,g4)
    c: PointOnObject(g5,g-2)
    c: Horizontal(g5)
    c: Coincident(g6,g5)
    c: Coincident(g6,g-1)
    c: Coincident(g7,g6)
    c: Coincident(g7,g0)
    c: DistanceX(g1,g4) = 28
    c: DistanceX(g0,g6) = 117
    c: Angle(g3,g4) = 2.35619
    c: DistanceY(g6,g6) = 4
    c: Distance(g7,g3) = 8
    c: DistanceX(g0,g0) = 5
    c: Vertical(g0,g2)
    c: Equal(g0,g2)
    c: DistanceY(g1,g1) = 4
    c: Coincident(g8,g9)
    c: Coincident(g9,g10)
    c: Coincident(g10,g11)
    c: Coincident(g11,g8)
    c: Vertical(g8)
    c: Vertical(g10)
    c: Horizontal(g9)
    c: Horizontal(g11)
FEATURE [PartDesign::Pocket] Pocket043
  BaseFeature = -> Pad045
  Direction = (-1,0,0)
  Length = 25
  Length2 = 5
  Midplane = true
  Profile = -> Sketch134
  ReferenceAxis = -> Sketch134 [N_Axis]
  Refine = true
  Suppressed = false
  Type = 0
FEATURE [PartDesign::Body] Body029  label="molle-clip"
  AllowCompound = false
  Group = -> [Sketch115,Pad045,Sketch134,Pocket043]
  Origin = -> Origin033
  Placement = pos=(-19,-87,24) rot=(0,0,1;3.14159rad)
  Tip = -> Pocket043
FEATURE [PartDesign::FeatureBase] Clone001
  BaseFeature = -> Body029
  Placement = pos=(-22,-87,24) rot=(0,0,1;3.14159rad)
  Suppressed = false
FEATURE [PartDesign::Body] Body030  label="molle-clip-clone-1"
  AllowCompound = false
  Group = -> [Clone001]
  Origin = -> Origin034
  Placement = pos=(41,0,0) rot=(0,0,1;0rad)
  Tip = -> Clone001
FEATURE [Sketcher::SketchObject] Sketch135
  ArcFitTolerance = 1e-06
  AttachmentSupport = -> [XZ_Plane055]
  FullyConstrained = false
  MakeInternals = false
  MapMode = 5
  Placement = pos=(0,0,0) rot=(1,0,0;1.5708rad)
  sketch-geometry (6):
    g0: LineSegment StartX=0 StartY=5 StartZ=0 EndX=3.6 EndY=5 EndZ=0
    g1: LineSegment StartX=3.6 StartY=5 StartZ=0 EndX=3.6 EndY=0 EndZ=0
    g2: LineSegment StartX=3.6 StartY=0 StartZ=0 EndX=2 EndY=0 EndZ=0
    g3: LineSegment StartX=2 StartY=0 StartZ=0 EndX=2 EndY=-8.67625 EndZ=0
    g4: LineSegment StartX=2 StartY=-8.67625 StartZ=0 EndX=0 EndY=-8.67625 EndZ=0
    g5: LineSegment StartX=0 StartY=-8.67625 StartZ=0 EndX=0 EndY=5 EndZ=0
  constraints (17):
    c: PointOnObject(g0,g-2)
    c: Horizontal(g0)
    c: Coincident(g1,g0)
    c: PointOnObject(g1,g-1)
    c: Vertical(g1)
    c: Coincident(g2,g1)
    c: PointOnObject(g2,g-1)
    c: Coincident(g3,g2)
    c: Vertical(g3)
    c: Coincident(g4,g3)
    c: PointOnObject(g4,g-2)
    c: Horizontal(g4)
    c: Coincident(g5,g4)
    c: Coincident(g5,g0)
    c: DistanceX(g0,g0) = 3.6
    c: DistanceX(g4,g4) = 2
    c: DistanceY(g1,g1) = 5
FEATURE [PartDesign::Revolution] Revolution006
  Angle = 360
  Angle2 = 60
  Axis = (0,2e-16,1)
  Base = (0,0,0)
  Placement = pos=(0,0,0) rot=(1,0,0;1.5708rad)
  Profile = -> Sketch135
  ReferenceAxis = -> Sketch135 [V_Axis]
  Refine = true
  Reversed = true
  Suppressed = false
  Type = 0
FEATURE [Sketcher::SketchObject] Sketch136
  ArcFitTolerance = 1e-06
  AttachmentOffset = pos=(0,0,5) rot=(0,0,1;0rad)
  AttachmentSupport = -> [XY_Plane055]
  FullyConstrained = true
  MakeInternals = false
  MapMode = 5
  Placement = pos=(0,0,5) rot=(0,0,1;0rad)
  sketch-geometry (7):
    g0: LineSegment StartX=1.5 StartY=0.866025 StartZ=0 EndX=2e-16 EndY=1.73205 EndZ=0
    g1: LineSegment StartX=2e-16 StartY=1.73205 StartZ=0 EndX=-1.5 EndY=0.866025 EndZ=0
    g2: LineSegment StartX=-1.5 StartY=0.866025 StartZ=0 EndX=-1.5 EndY=-0.866025 EndZ=0
    g3: LineSegment StartX=-1.5 StartY=-0.866025 StartZ=0 EndX=-2e-16 EndY=-1.73205 EndZ=0
    g4: LineSegment StartX=-2e-16 StartY=-1.73205 StartZ=0 EndX=1.5 EndY=-0.866025 EndZ=0
    g5: LineSegment StartX=1.5 StartY=-0.866025 StartZ=0 EndX=1.5 EndY=0.866025 EndZ=0
    g6: Circle [constr] CenterX=0 CenterY=0 CenterZ=0 NormalX=0 NormalY=0 NormalZ=1 AngleXU=0 Radius=1.73205
  constraints (16):
    c: Coincident(g0,g1)
    c: Coincident(g1,g2)
    c: Coincident(g2,g3)
    c: Coincident(g3,g4)
    c: Coincident(g4,g5)
    c: Coincident(g5,g0)
    c: Equal(g0, g1-g5) x5
    c: PointOnObject(g0,g6)
    c: PointOnObject(g1,g6)
    c: PointOnObject(g2,g6)
    c: PointOnObject(g3,g6)
    c: PointOnObject(g4,g6)
    c: PointOnObject(g5,g6)
    c: Coincident(g6,g-1)
    c: Vertical(g5)
    c: DistanceX(g1,g0) = 3
FEATURE [PartDesign::Pocket] Pocket044
  BaseFeature = -> Revolution006
  Direction = (0,0,-1)
  Length = 2
  Length2 = 5
  Placement = pos=(0,0,0) rot=(1,0,0;1.5708rad)
  Profile = -> Sketch136
  ReferenceAxis = -> Sketch136 [N_Axis]
  Refine = true
  Suppressed = false
  Type = 0
FEATURE [PartDesign::Body] Body050  label="bolt-m4-l10"
  AllowCompound = false
  Group = -> [Sketch135,Revolution006,Sketch136,Pocket044]
  Origin = -> Origin055
  Tip = -> Pocket044
PROVENANCE & LICENSES
A FreeCAD (.FCStd) document from a public repository crawl; recipes are the document's own serialized feature recipes (and, for linked parts, companion documents' recipes).
License: as declared in the source repository (recorded in the dataset sidecar).
